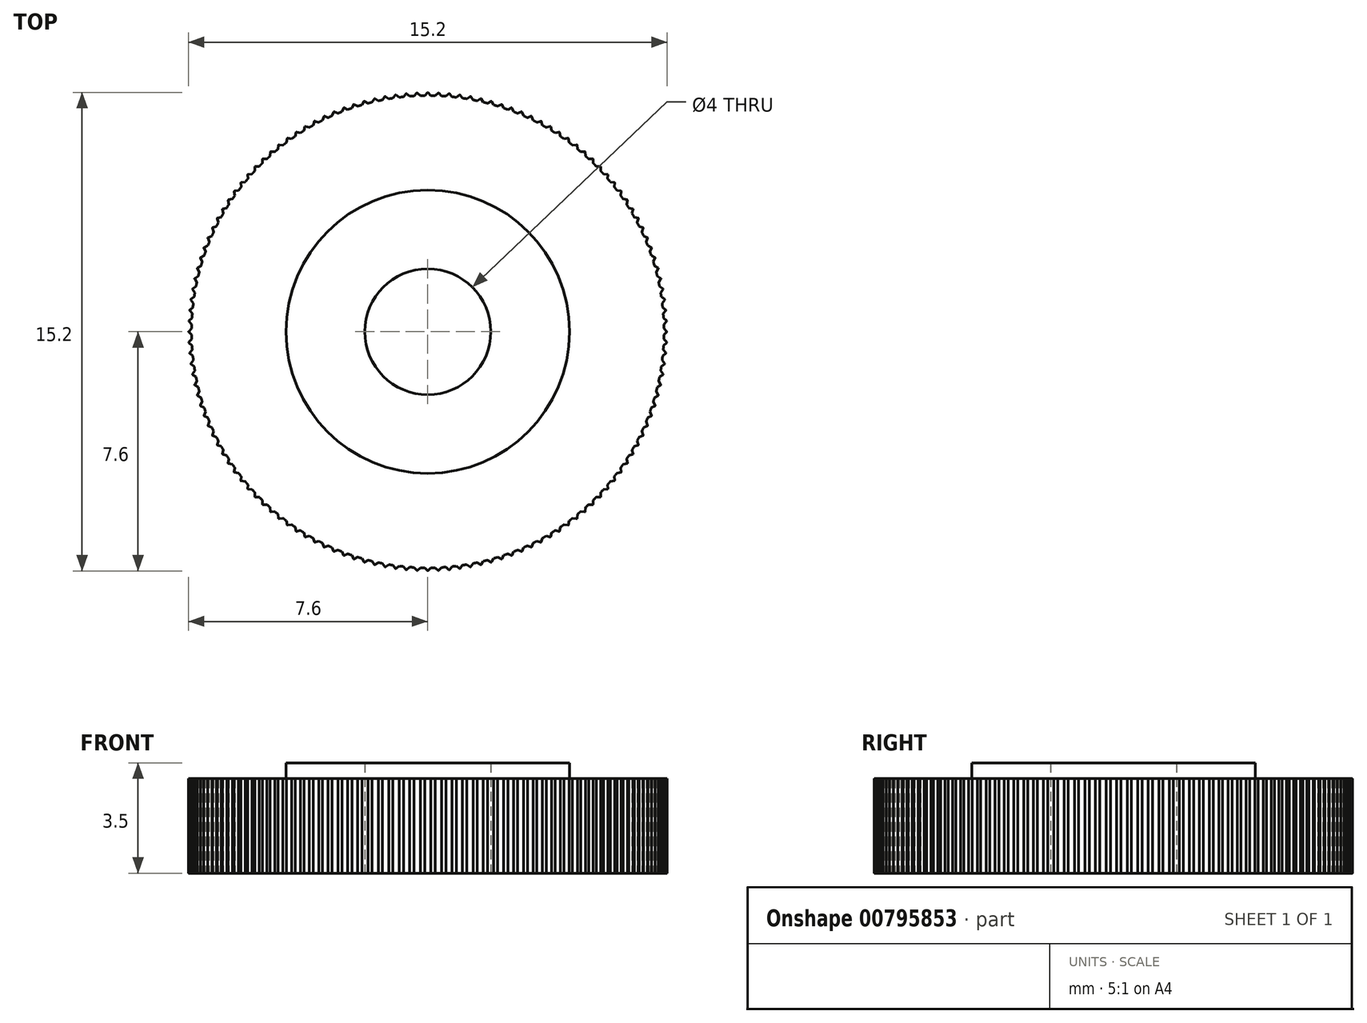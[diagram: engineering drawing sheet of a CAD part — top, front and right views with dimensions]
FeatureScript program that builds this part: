
annotation { "Feature Type Name" : "Feature", "Feature Type Description" : "" }
export const myFeature = defineFeature(function(context is Context, id is Id, definition is map)
    precondition{}
    {
        {
            var Q0;
            Q0=qCreatedBy(makeId("Top.planeOp"),FACE);
            var sketch = newSketch(context, id + "F0", { "sketchPlane" : qUnion([Q0])});
            skCircle(sketch, "E0", {"center": v(0, 0) * mm, "radius": 2 * mm});
            skCircle(sketch, "E1", {"center": v(0, 0) * mm, "radius": 7.5 * mm});
            skArc(sketch, "E2", {"start": v(-0.1, 7.5) * mm, "mid": v(0, 7.5) * mm, "end": v(0.1, 7.5) * mm});
            skLineSegment(sketch, "E3", {"start": v(-0.1, 7.5) * mm, "end": v(0, 7.6) * mm});
            skLineSegment(sketch, "E4", {"start": v(0.1, 7.5) * mm, "end": v(0, 7.6) * mm});
            skPoint(sketch, "E5.visualSharp", {"position": v(0, 7.6) * mm});
            skArc(sketch, "E5.filletArc", {"start": v(0, 7.6) * mm, "mid": v(0, 7.6) * mm, "end": v(0, 7.6) * mm});
            skPoint(sketch, "E6.1.0", {"position": v(-6.58, -3.8) * mm});
            skArc(sketch, "E6.1.1", {"start": v(-6.58, -3.79) * mm, "mid": v(-6.58, -3.8) * mm, "end": v(-6.57, -3.8) * mm});
            skArc(sketch, "E6.2.1", {"start": v(6.57, -3.8) * mm, "mid": v(6.58, -3.8) * mm, "end": v(6.58, -3.79) * mm});
            skLineSegment(sketch, "E7.1.0", {"start": v(-0.44, 7.49) * mm, "end": v(-0.35, 7.58) * mm});
            skArc(sketch, "E7.1.1", {"start": v(-0.44, 7.49) * mm, "mid": v(-0.34, 7.5) * mm, "end": v(-0.24, 7.5) * mm});
            skLineSegment(sketch, "E7.1.2", {"start": v(-0.24, 7.5) * mm, "end": v(-0.33, 7.58) * mm});
            skPoint(sketch, "E7.1.3", {"position": v(-0.34, 7.6) * mm});
            skArc(sketch, "E7.1.4", {"start": v(-0.33, 7.58) * mm, "mid": v(-0.34, 7.59) * mm, "end": v(-0.35, 7.58) * mm});
            skLineSegment(sketch, "E7.2.0", {"start": v(-0.77, 7.46) * mm, "end": v(-0.69, 7.56) * mm});
            skArc(sketch, "E7.2.1", {"start": v(-0.77, 7.46) * mm, "mid": v(-0.67, 7.47) * mm, "end": v(-0.57, 7.48) * mm});
            skLineSegment(sketch, "E7.2.2", {"start": v(-0.57, 7.48) * mm, "end": v(-0.67, 7.56) * mm});
            skPoint(sketch, "E7.2.3", {"position": v(-0.68, 7.57) * mm});
            skArc(sketch, "E7.2.4", {"start": v(-0.67, 7.56) * mm, "mid": v(-0.68, 7.56) * mm, "end": v(-0.69, 7.56) * mm});
            skLineSegment(sketch, "E7.3.0", {"start": v(-1.1, 7.42) * mm, "end": v(-1.03, 7.52) * mm});
            skArc(sketch, "E7.3.1", {"start": v(-1.1, 7.42) * mm, "mid": v(-1, 7.43) * mm, "end": v(-0.9, 7.44) * mm});
            skLineSegment(sketch, "E7.3.2", {"start": v(-0.9, 7.44) * mm, "end": v(-1.01, 7.52) * mm});
            skPoint(sketch, "E7.3.3", {"position": v(-1.02, 7.53) * mm});
            skArc(sketch, "E7.3.4", {"start": v(-1.01, 7.52) * mm, "mid": v(-1.02, 7.53) * mm, "end": v(-1.03, 7.52) * mm});
            skLineSegment(sketch, "E7.4.0", {"start": v(-1.44, 7.36) * mm, "end": v(-1.36, 7.47) * mm});
            skArc(sketch, "E7.4.1", {"start": v(-1.44, 7.36) * mm, "mid": v(-1.34, 7.38) * mm, "end": v(-1.24, 7.4) * mm});
            skLineSegment(sketch, "E7.4.2", {"start": v(-1.24, 7.4) * mm, "end": v(-1.35, 7.47) * mm});
            skPoint(sketch, "E7.4.3", {"position": v(-1.36, 7.48) * mm});
            skArc(sketch, "E7.4.4", {"start": v(-1.35, 7.47) * mm, "mid": v(-1.36, 7.47) * mm, "end": v(-1.36, 7.47) * mm});
            skLineSegment(sketch, "E7.5.0", {"start": v(-1.77, 7.29) * mm, "end": v(-1.7, 7.4) * mm});
            skArc(sketch, "E7.5.1", {"start": v(-1.77, 7.29) * mm, "mid": v(-1.67, 7.31) * mm, "end": v(-1.57, 7.33) * mm});
            skLineSegment(sketch, "E7.5.2", {"start": v(-1.57, 7.33) * mm, "end": v(-1.68, 7.4) * mm});
            skPoint(sketch, "E7.5.3", {"position": v(-1.7, 7.4) * mm});
            skArc(sketch, "E7.5.4", {"start": v(-1.68, 7.4) * mm, "mid": v(-1.7, 7.4) * mm, "end": v(-1.7, 7.4) * mm});
            skLineSegment(sketch, "E7.6.0", {"start": v(-2.1, 7.2) * mm, "end": v(-2.03, 7.32) * mm});
            skArc(sketch, "E7.6.1", {"start": v(-2.1, 7.2) * mm, "mid": v(-2, 7.23) * mm, "end": v(-1.9, 7.26) * mm});
            skLineSegment(sketch, "E7.6.2", {"start": v(-1.9, 7.26) * mm, "end": v(-2.01, 7.32) * mm});
            skPoint(sketch, "E7.6.3", {"position": v(-2.02, 7.33) * mm});
            skArc(sketch, "E7.6.4", {"start": v(-2.01, 7.32) * mm, "mid": v(-2.02, 7.32) * mm, "end": v(-2.03, 7.32) * mm});
            skLineSegment(sketch, "E7.7.0", {"start": v(-2.41, 7.1) * mm, "end": v(-2.35, 7.22) * mm});
            skArc(sketch, "E7.7.1", {"start": v(-2.41, 7.1) * mm, "mid": v(-2.32, 7.13) * mm, "end": v(-2.22, 7.16) * mm});
            skLineSegment(sketch, "E7.7.2", {"start": v(-2.22, 7.16) * mm, "end": v(-2.34, 7.22) * mm});
            skPoint(sketch, "E7.7.3", {"position": v(-2.35, 7.23) * mm});
            skArc(sketch, "E7.7.4", {"start": v(-2.34, 7.22) * mm, "mid": v(-2.35, 7.22) * mm, "end": v(-2.35, 7.22) * mm});
            skLineSegment(sketch, "E7.8.0", {"start": v(-2.73, 6.99) * mm, "end": v(-2.68, 7.1) * mm});
            skArc(sketch, "E7.8.1", {"start": v(-2.73, 6.99) * mm, "mid": v(-2.64, 7.02) * mm, "end": v(-2.54, 7.06) * mm});
            skLineSegment(sketch, "E7.8.2", {"start": v(-2.54, 7.06) * mm, "end": v(-2.66, 7.11) * mm});
            skPoint(sketch, "E7.8.3", {"position": v(-2.67, 7.12) * mm});
            skArc(sketch, "E7.8.4", {"start": v(-2.66, 7.11) * mm, "mid": v(-2.67, 7.11) * mm, "end": v(-2.68, 7.1) * mm});
            skLineSegment(sketch, "E7.9.0", {"start": v(-3.04, 6.86) * mm, "end": v(-3, 6.98) * mm});
            skArc(sketch, "E7.9.1", {"start": v(-3.04, 6.86) * mm, "mid": v(-2.95, 6.9) * mm, "end": v(-2.86, 6.94) * mm});
            skLineSegment(sketch, "E7.9.2", {"start": v(-2.86, 6.94) * mm, "end": v(-2.98, 6.98) * mm});
            skPoint(sketch, "E7.9.3", {"position": v(-2.99, 6.99) * mm});
            skArc(sketch, "E7.9.4", {"start": v(-2.98, 6.98) * mm, "mid": v(-2.99, 6.98) * mm, "end": v(-3, 6.98) * mm});
            skLineSegment(sketch, "E7.10.0", {"start": v(-3.34, 6.71) * mm, "end": v(-3.3, 6.84) * mm});
            skArc(sketch, "E7.10.1", {"start": v(-3.34, 6.71) * mm, "mid": v(-3.25, 6.76) * mm, "end": v(-3.16, 6.8) * mm});
            skLineSegment(sketch, "E7.10.2", {"start": v(-3.16, 6.8) * mm, "end": v(-3.29, 6.84) * mm});
            skPoint(sketch, "E7.10.3", {"position": v(-3.3, 6.85) * mm});
            skArc(sketch, "E7.10.4", {"start": v(-3.29, 6.84) * mm, "mid": v(-3.3, 6.84) * mm, "end": v(-3.3, 6.84) * mm});
            skLineSegment(sketch, "E7.11.0", {"start": v(-3.64, 6.56) * mm, "end": v(-3.6, 6.68) * mm});
            skArc(sketch, "E7.11.1", {"start": v(-3.64, 6.56) * mm, "mid": v(-3.55, 6.6) * mm, "end": v(-3.47, 6.65) * mm});
            skLineSegment(sketch, "E7.11.2", {"start": v(-3.47, 6.65) * mm, "end": v(-3.6, 6.69) * mm});
            skPoint(sketch, "E7.11.3", {"position": v(-3.6, 6.7) * mm});
            skArc(sketch, "E7.11.4", {"start": v(-3.6, 6.69) * mm, "mid": v(-3.6, 6.69) * mm, "end": v(-3.6, 6.68) * mm});
            skLineSegment(sketch, "E7.12.0", {"start": v(-3.93, 6.39) * mm, "end": v(-3.9, 6.51) * mm});
            skArc(sketch, "E7.12.1", {"start": v(-3.93, 6.39) * mm, "mid": v(-3.85, 6.44) * mm, "end": v(-3.76, 6.49) * mm});
            skLineSegment(sketch, "E7.12.2", {"start": v(-3.76, 6.49) * mm, "end": v(-3.89, 6.52) * mm});
            skPoint(sketch, "E7.12.3", {"position": v(-3.9, 6.52) * mm});
            skArc(sketch, "E7.12.4", {"start": v(-3.89, 6.52) * mm, "mid": v(-3.9, 6.52) * mm, "end": v(-3.9, 6.51) * mm});
            skLineSegment(sketch, "E7.13.0", {"start": v(-4.21, 6.2) * mm, "end": v(-4.19, 6.33) * mm});
            skArc(sketch, "E7.13.1", {"start": v(-4.21, 6.2) * mm, "mid": v(-4.13, 6.26) * mm, "end": v(-4.05, 6.31) * mm});
            skLineSegment(sketch, "E7.13.2", {"start": v(-4.05, 6.31) * mm, "end": v(-4.18, 6.34) * mm});
            skPoint(sketch, "E7.13.3", {"position": v(-4.19, 6.34) * mm});
            skArc(sketch, "E7.13.4", {"start": v(-4.18, 6.34) * mm, "mid": v(-4.18, 6.34) * mm, "end": v(-4.19, 6.33) * mm});
            skLineSegment(sketch, "E7.14.0", {"start": v(-4.49, 6) * mm, "end": v(-4.47, 6.14) * mm});
            skArc(sketch, "E7.14.1", {"start": v(-4.49, 6) * mm, "mid": v(-4.4, 6.07) * mm, "end": v(-4.33, 6.13) * mm});
            skLineSegment(sketch, "E7.14.2", {"start": v(-4.33, 6.13) * mm, "end": v(-4.46, 6.15) * mm});
            skPoint(sketch, "E7.14.3", {"position": v(-4.47, 6.15) * mm});
            skArc(sketch, "E7.14.4", {"start": v(-4.46, 6.15) * mm, "mid": v(-4.46, 6.14) * mm, "end": v(-4.47, 6.14) * mm});
            skLineSegment(sketch, "E7.15.0", {"start": v(-4.75, 5.8) * mm, "end": v(-4.74, 5.93) * mm});
            skArc(sketch, "E7.15.1", {"start": v(-4.75, 5.8) * mm, "mid": v(-4.68, 5.86) * mm, "end": v(-4.6, 5.93) * mm});
            skLineSegment(sketch, "E7.15.2", {"start": v(-4.6, 5.93) * mm, "end": v(-4.73, 5.94) * mm});
            skPoint(sketch, "E7.15.3", {"position": v(-4.74, 5.94) * mm});
            skArc(sketch, "E7.15.4", {"start": v(-4.73, 5.94) * mm, "mid": v(-4.74, 5.94) * mm, "end": v(-4.74, 5.93) * mm});
            skLineSegment(sketch, "E7.16.0", {"start": v(-5, 5.58) * mm, "end": v(-5, 5.71) * mm});
            skArc(sketch, "E7.16.1", {"start": v(-5, 5.58) * mm, "mid": v(-4.93, 5.65) * mm, "end": v(-4.86, 5.71) * mm});
            skLineSegment(sketch, "E7.16.2", {"start": v(-4.86, 5.71) * mm, "end": v(-4.99, 5.72) * mm});
            skPoint(sketch, "E7.16.3", {"position": v(-5, 5.72) * mm});
            skArc(sketch, "E7.16.4", {"start": v(-4.99, 5.72) * mm, "mid": v(-5, 5.72) * mm, "end": v(-5, 5.71) * mm});
            skLineSegment(sketch, "E7.17.0", {"start": v(-5.25, 5.35) * mm, "end": v(-5.25, 5.48) * mm});
            skArc(sketch, "E7.17.1", {"start": v(-5.25, 5.35) * mm, "mid": v(-5.18, 5.42) * mm, "end": v(-5.11, 5.49) * mm});
            skLineSegment(sketch, "E7.17.2", {"start": v(-5.11, 5.49) * mm, "end": v(-5.24, 5.5) * mm});
            skPoint(sketch, "E7.17.3", {"position": v(-5.25, 5.5) * mm});
            skArc(sketch, "E7.17.4", {"start": v(-5.24, 5.5) * mm, "mid": v(-5.25, 5.49) * mm, "end": v(-5.25, 5.48) * mm});
            skLineSegment(sketch, "E7.18.0", {"start": v(-5.49, 5.11) * mm, "end": v(-5.5, 5.24) * mm});
            skArc(sketch, "E7.18.1", {"start": v(-5.49, 5.11) * mm, "mid": v(-5.42, 5.18) * mm, "end": v(-5.35, 5.25) * mm});
            skLineSegment(sketch, "E7.18.2", {"start": v(-5.35, 5.25) * mm, "end": v(-5.48, 5.25) * mm});
            skPoint(sketch, "E7.18.3", {"position": v(-5.5, 5.25) * mm});
            skArc(sketch, "E7.18.4", {"start": v(-5.48, 5.25) * mm, "mid": v(-5.49, 5.25) * mm, "end": v(-5.5, 5.24) * mm});
            skLineSegment(sketch, "E7.19.0", {"start": v(-5.71, 4.86) * mm, "end": v(-5.72, 4.99) * mm});
            skArc(sketch, "E7.19.1", {"start": v(-5.71, 4.86) * mm, "mid": v(-5.65, 4.93) * mm, "end": v(-5.58, 5) * mm});
            skLineSegment(sketch, "E7.19.2", {"start": v(-5.58, 5) * mm, "end": v(-5.71, 5) * mm});
            skPoint(sketch, "E7.19.3", {"position": v(-5.72, 5) * mm});
            skArc(sketch, "E7.19.4", {"start": v(-5.71, 5) * mm, "mid": v(-5.72, 5) * mm, "end": v(-5.72, 4.99) * mm});
            skLineSegment(sketch, "E7.20.0", {"start": v(-5.93, 4.6) * mm, "end": v(-5.94, 4.73) * mm});
            skArc(sketch, "E7.20.1", {"start": v(-5.93, 4.6) * mm, "mid": v(-5.86, 4.68) * mm, "end": v(-5.8, 4.75) * mm});
            skLineSegment(sketch, "E7.20.2", {"start": v(-5.8, 4.75) * mm, "end": v(-5.93, 4.74) * mm});
            skPoint(sketch, "E7.20.3", {"position": v(-5.94, 4.74) * mm});
            skArc(sketch, "E7.20.4", {"start": v(-5.93, 4.74) * mm, "mid": v(-5.94, 4.74) * mm, "end": v(-5.94, 4.73) * mm});
            skLineSegment(sketch, "E7.21.0", {"start": v(-6.13, 4.33) * mm, "end": v(-6.15, 4.46) * mm});
            skArc(sketch, "E7.21.1", {"start": v(-6.13, 4.33) * mm, "mid": v(-6.07, 4.4) * mm, "end": v(-6, 4.49) * mm});
            skLineSegment(sketch, "E7.21.2", {"start": v(-6, 4.49) * mm, "end": v(-6.14, 4.47) * mm});
            skPoint(sketch, "E7.21.3", {"position": v(-6.15, 4.47) * mm});
            skArc(sketch, "E7.21.4", {"start": v(-6.14, 4.47) * mm, "mid": v(-6.14, 4.46) * mm, "end": v(-6.15, 4.46) * mm});
            skLineSegment(sketch, "E7.22.0", {"start": v(-6.31, 4.05) * mm, "end": v(-6.34, 4.18) * mm});
            skArc(sketch, "E7.22.1", {"start": v(-6.31, 4.05) * mm, "mid": v(-6.26, 4.13) * mm, "end": v(-6.2, 4.21) * mm});
            skLineSegment(sketch, "E7.22.2", {"start": v(-6.2, 4.21) * mm, "end": v(-6.33, 4.19) * mm});
            skPoint(sketch, "E7.22.3", {"position": v(-6.34, 4.19) * mm});
            skArc(sketch, "E7.22.4", {"start": v(-6.33, 4.19) * mm, "mid": v(-6.34, 4.18) * mm, "end": v(-6.34, 4.18) * mm});
            skLineSegment(sketch, "E7.23.0", {"start": v(-6.49, 3.76) * mm, "end": v(-6.52, 3.89) * mm});
            skArc(sketch, "E7.23.1", {"start": v(-6.49, 3.76) * mm, "mid": v(-6.44, 3.85) * mm, "end": v(-6.39, 3.93) * mm});
            skLineSegment(sketch, "E7.23.2", {"start": v(-6.39, 3.93) * mm, "end": v(-6.51, 3.9) * mm});
            skPoint(sketch, "E7.23.3", {"position": v(-6.52, 3.9) * mm});
            skArc(sketch, "E7.23.4", {"start": v(-6.51, 3.9) * mm, "mid": v(-6.52, 3.9) * mm, "end": v(-6.52, 3.89) * mm});
            skLineSegment(sketch, "E7.24.0", {"start": v(-6.65, 3.47) * mm, "end": v(-6.69, 3.6) * mm});
            skArc(sketch, "E7.24.1", {"start": v(-6.65, 3.47) * mm, "mid": v(-6.6, 3.55) * mm, "end": v(-6.56, 3.64) * mm});
            skLineSegment(sketch, "E7.24.2", {"start": v(-6.56, 3.64) * mm, "end": v(-6.68, 3.6) * mm});
            skPoint(sketch, "E7.24.3", {"position": v(-6.7, 3.6) * mm});
            skArc(sketch, "E7.24.4", {"start": v(-6.68, 3.6) * mm, "mid": v(-6.69, 3.6) * mm, "end": v(-6.69, 3.6) * mm});
            skLineSegment(sketch, "E7.25.0", {"start": v(-6.8, 3.16) * mm, "end": v(-6.84, 3.29) * mm});
            skArc(sketch, "E7.25.1", {"start": v(-6.8, 3.16) * mm, "mid": v(-6.76, 3.25) * mm, "end": v(-6.71, 3.34) * mm});
            skLineSegment(sketch, "E7.25.2", {"start": v(-6.71, 3.34) * mm, "end": v(-6.84, 3.3) * mm});
            skPoint(sketch, "E7.25.3", {"position": v(-6.85, 3.3) * mm});
            skArc(sketch, "E7.25.4", {"start": v(-6.84, 3.3) * mm, "mid": v(-6.84, 3.3) * mm, "end": v(-6.84, 3.29) * mm});
            skLineSegment(sketch, "E7.26.0", {"start": v(-6.94, 2.86) * mm, "end": v(-6.98, 2.98) * mm});
            skArc(sketch, "E7.26.1", {"start": v(-6.94, 2.86) * mm, "mid": v(-6.9, 2.95) * mm, "end": v(-6.86, 3.04) * mm});
            skLineSegment(sketch, "E7.26.2", {"start": v(-6.86, 3.04) * mm, "end": v(-6.98, 3) * mm});
            skPoint(sketch, "E7.26.3", {"position": v(-6.99, 2.99) * mm});
            skArc(sketch, "E7.26.4", {"start": v(-6.98, 3) * mm, "mid": v(-6.98, 2.99) * mm, "end": v(-6.98, 2.98) * mm});
            skLineSegment(sketch, "E7.27.0", {"start": v(-7.06, 2.54) * mm, "end": v(-7.11, 2.66) * mm});
            skArc(sketch, "E7.27.1", {"start": v(-7.06, 2.54) * mm, "mid": v(-7.02, 2.64) * mm, "end": v(-6.99, 2.73) * mm});
            skLineSegment(sketch, "E7.27.2", {"start": v(-6.99, 2.73) * mm, "end": v(-7.1, 2.68) * mm});
            skPoint(sketch, "E7.27.3", {"position": v(-7.12, 2.67) * mm});
            skArc(sketch, "E7.27.4", {"start": v(-7.1, 2.68) * mm, "mid": v(-7.11, 2.67) * mm, "end": v(-7.11, 2.66) * mm});
            skLineSegment(sketch, "E7.28.0", {"start": v(-7.16, 2.22) * mm, "end": v(-7.22, 2.34) * mm});
            skArc(sketch, "E7.28.1", {"start": v(-7.16, 2.22) * mm, "mid": v(-7.13, 2.32) * mm, "end": v(-7.1, 2.41) * mm});
            skLineSegment(sketch, "E7.28.2", {"start": v(-7.1, 2.41) * mm, "end": v(-7.22, 2.35) * mm});
            skPoint(sketch, "E7.28.3", {"position": v(-7.23, 2.35) * mm});
            skArc(sketch, "E7.28.4", {"start": v(-7.22, 2.35) * mm, "mid": v(-7.22, 2.35) * mm, "end": v(-7.22, 2.34) * mm});
            skLineSegment(sketch, "E7.29.0", {"start": v(-7.26, 1.9) * mm, "end": v(-7.32, 2.01) * mm});
            skArc(sketch, "E7.29.1", {"start": v(-7.26, 1.9) * mm, "mid": v(-7.23, 2) * mm, "end": v(-7.2, 2.1) * mm});
            skLineSegment(sketch, "E7.29.2", {"start": v(-7.2, 2.1) * mm, "end": v(-7.32, 2.03) * mm});
            skPoint(sketch, "E7.29.3", {"position": v(-7.33, 2.02) * mm});
            skArc(sketch, "E7.29.4", {"start": v(-7.32, 2.03) * mm, "mid": v(-7.32, 2.02) * mm, "end": v(-7.32, 2.01) * mm});
            skLineSegment(sketch, "E7.30.0", {"start": v(-7.33, 1.57) * mm, "end": v(-7.4, 1.68) * mm});
            skArc(sketch, "E7.30.1", {"start": v(-7.33, 1.57) * mm, "mid": v(-7.31, 1.67) * mm, "end": v(-7.29, 1.77) * mm});
            skLineSegment(sketch, "E7.30.2", {"start": v(-7.29, 1.77) * mm, "end": v(-7.4, 1.7) * mm});
            skPoint(sketch, "E7.30.3", {"position": v(-7.4, 1.7) * mm});
            skArc(sketch, "E7.30.4", {"start": v(-7.4, 1.7) * mm, "mid": v(-7.4, 1.7) * mm, "end": v(-7.4, 1.68) * mm});
            skLineSegment(sketch, "E7.31.0", {"start": v(-7.4, 1.24) * mm, "end": v(-7.47, 1.35) * mm});
            skArc(sketch, "E7.31.1", {"start": v(-7.4, 1.24) * mm, "mid": v(-7.38, 1.34) * mm, "end": v(-7.36, 1.44) * mm});
            skLineSegment(sketch, "E7.31.2", {"start": v(-7.36, 1.44) * mm, "end": v(-7.47, 1.36) * mm});
            skPoint(sketch, "E7.31.3", {"position": v(-7.48, 1.36) * mm});
            skArc(sketch, "E7.31.4", {"start": v(-7.47, 1.36) * mm, "mid": v(-7.47, 1.36) * mm, "end": v(-7.47, 1.35) * mm});
            skLineSegment(sketch, "E7.32.0", {"start": v(-7.44, 0.9) * mm, "end": v(-7.52, 1.01) * mm});
            skArc(sketch, "E7.32.1", {"start": v(-7.44, 0.9) * mm, "mid": v(-7.43, 1) * mm, "end": v(-7.42, 1.1) * mm});
            skLineSegment(sketch, "E7.32.2", {"start": v(-7.42, 1.1) * mm, "end": v(-7.52, 1.03) * mm});
            skPoint(sketch, "E7.32.3", {"position": v(-7.53, 1.02) * mm});
            skArc(sketch, "E7.32.4", {"start": v(-7.52, 1.03) * mm, "mid": v(-7.53, 1.02) * mm, "end": v(-7.52, 1.01) * mm});
            skLineSegment(sketch, "E7.33.0", {"start": v(-7.48, 0.57) * mm, "end": v(-7.56, 0.67) * mm});
            skArc(sketch, "E7.33.1", {"start": v(-7.48, 0.57) * mm, "mid": v(-7.47, 0.67) * mm, "end": v(-7.46, 0.77) * mm});
            skLineSegment(sketch, "E7.33.2", {"start": v(-7.46, 0.77) * mm, "end": v(-7.56, 0.69) * mm});
            skPoint(sketch, "E7.33.3", {"position": v(-7.57, 0.68) * mm});
            skArc(sketch, "E7.33.4", {"start": v(-7.56, 0.69) * mm, "mid": v(-7.56, 0.68) * mm, "end": v(-7.56, 0.67) * mm});
            skLineSegment(sketch, "E7.34.0", {"start": v(-7.5, 0.24) * mm, "end": v(-7.58, 0.33) * mm});
            skArc(sketch, "E7.34.1", {"start": v(-7.5, 0.24) * mm, "mid": v(-7.5, 0.34) * mm, "end": v(-7.49, 0.44) * mm});
            skLineSegment(sketch, "E7.34.2", {"start": v(-7.49, 0.44) * mm, "end": v(-7.58, 0.35) * mm});
            skPoint(sketch, "E7.34.3", {"position": v(-7.6, 0.34) * mm});
            skArc(sketch, "E7.34.4", {"start": v(-7.58, 0.35) * mm, "mid": v(-7.59, 0.34) * mm, "end": v(-7.58, 0.33) * mm});
            skLineSegment(sketch, "E7.35.0", {"start": v(-7.5, -0.1) * mm, "end": v(-7.6, 0) * mm});
            skArc(sketch, "E7.35.1", {"start": v(-7.5, -0.1) * mm, "mid": v(-7.5, 0) * mm, "end": v(-7.5, 0.1) * mm});
            skLineSegment(sketch, "E7.35.2", {"start": v(-7.5, 0.1) * mm, "end": v(-7.6, 0) * mm});
            skPoint(sketch, "E7.35.3", {"position": v(-7.6, 0) * mm});
            skArc(sketch, "E7.35.4", {"start": v(-7.6, 0) * mm, "mid": v(-7.6, 0) * mm, "end": v(-7.6, 0) * mm});
            skLineSegment(sketch, "E7.36.0", {"start": v(-7.49, -0.44) * mm, "end": v(-7.58, -0.35) * mm});
            skArc(sketch, "E7.36.1", {"start": v(-7.49, -0.44) * mm, "mid": v(-7.5, -0.34) * mm, "end": v(-7.5, -0.24) * mm});
            skLineSegment(sketch, "E7.36.2", {"start": v(-7.5, -0.24) * mm, "end": v(-7.58, -0.33) * mm});
            skPoint(sketch, "E7.36.3", {"position": v(-7.6, -0.34) * mm});
            skArc(sketch, "E7.36.4", {"start": v(-7.58, -0.33) * mm, "mid": v(-7.59, -0.34) * mm, "end": v(-7.58, -0.35) * mm});
            skLineSegment(sketch, "E7.37.0", {"start": v(-7.46, -0.77) * mm, "end": v(-7.56, -0.69) * mm});
            skArc(sketch, "E7.37.1", {"start": v(-7.46, -0.77) * mm, "mid": v(-7.47, -0.67) * mm, "end": v(-7.48, -0.57) * mm});
            skLineSegment(sketch, "E7.37.2", {"start": v(-7.48, -0.57) * mm, "end": v(-7.56, -0.67) * mm});
            skPoint(sketch, "E7.37.3", {"position": v(-7.57, -0.68) * mm});
            skArc(sketch, "E7.37.4", {"start": v(-7.56, -0.67) * mm, "mid": v(-7.56, -0.68) * mm, "end": v(-7.56, -0.69) * mm});
            skLineSegment(sketch, "E7.38.0", {"start": v(-7.42, -1.1) * mm, "end": v(-7.52, -1.03) * mm});
            skArc(sketch, "E7.38.1", {"start": v(-7.42, -1.1) * mm, "mid": v(-7.43, -1) * mm, "end": v(-7.44, -0.9) * mm});
            skLineSegment(sketch, "E7.38.2", {"start": v(-7.44, -0.9) * mm, "end": v(-7.52, -1.01) * mm});
            skPoint(sketch, "E7.38.3", {"position": v(-7.53, -1.02) * mm});
            skArc(sketch, "E7.38.4", {"start": v(-7.52, -1.01) * mm, "mid": v(-7.53, -1.02) * mm, "end": v(-7.52, -1.03) * mm});
            skLineSegment(sketch, "E7.39.0", {"start": v(-7.36, -1.44) * mm, "end": v(-7.47, -1.36) * mm});
            skArc(sketch, "E7.39.1", {"start": v(-7.36, -1.44) * mm, "mid": v(-7.38, -1.34) * mm, "end": v(-7.4, -1.24) * mm});
            skLineSegment(sketch, "E7.39.2", {"start": v(-7.4, -1.24) * mm, "end": v(-7.47, -1.35) * mm});
            skPoint(sketch, "E7.39.3", {"position": v(-7.48, -1.36) * mm});
            skArc(sketch, "E7.39.4", {"start": v(-7.47, -1.35) * mm, "mid": v(-7.47, -1.36) * mm, "end": v(-7.47, -1.36) * mm});
            skLineSegment(sketch, "E7.40.0", {"start": v(-7.29, -1.77) * mm, "end": v(-7.4, -1.7) * mm});
            skArc(sketch, "E7.40.1", {"start": v(-7.29, -1.77) * mm, "mid": v(-7.31, -1.67) * mm, "end": v(-7.33, -1.57) * mm});
            skLineSegment(sketch, "E7.40.2", {"start": v(-7.33, -1.57) * mm, "end": v(-7.4, -1.68) * mm});
            skPoint(sketch, "E7.40.3", {"position": v(-7.4, -1.7) * mm});
            skArc(sketch, "E7.40.4", {"start": v(-7.4, -1.68) * mm, "mid": v(-7.4, -1.7) * mm, "end": v(-7.4, -1.7) * mm});
            skLineSegment(sketch, "E7.41.0", {"start": v(-7.2, -2.1) * mm, "end": v(-7.32, -2.03) * mm});
            skArc(sketch, "E7.41.1", {"start": v(-7.2, -2.1) * mm, "mid": v(-7.23, -2) * mm, "end": v(-7.26, -1.9) * mm});
            skLineSegment(sketch, "E7.41.2", {"start": v(-7.26, -1.9) * mm, "end": v(-7.32, -2.01) * mm});
            skPoint(sketch, "E7.41.3", {"position": v(-7.33, -2.02) * mm});
            skArc(sketch, "E7.41.4", {"start": v(-7.32, -2.01) * mm, "mid": v(-7.32, -2.02) * mm, "end": v(-7.32, -2.03) * mm});
            skLineSegment(sketch, "E7.42.0", {"start": v(-7.1, -2.41) * mm, "end": v(-7.22, -2.35) * mm});
            skArc(sketch, "E7.42.1", {"start": v(-7.1, -2.41) * mm, "mid": v(-7.13, -2.32) * mm, "end": v(-7.16, -2.22) * mm});
            skLineSegment(sketch, "E7.42.2", {"start": v(-7.16, -2.22) * mm, "end": v(-7.22, -2.34) * mm});
            skPoint(sketch, "E7.42.3", {"position": v(-7.23, -2.35) * mm});
            skArc(sketch, "E7.42.4", {"start": v(-7.22, -2.34) * mm, "mid": v(-7.22, -2.35) * mm, "end": v(-7.22, -2.35) * mm});
            skLineSegment(sketch, "E7.43.0", {"start": v(-6.99, -2.73) * mm, "end": v(-7.1, -2.68) * mm});
            skArc(sketch, "E7.43.1", {"start": v(-6.99, -2.73) * mm, "mid": v(-7.02, -2.64) * mm, "end": v(-7.06, -2.54) * mm});
            skLineSegment(sketch, "E7.43.2", {"start": v(-7.06, -2.54) * mm, "end": v(-7.11, -2.66) * mm});
            skPoint(sketch, "E7.43.3", {"position": v(-7.12, -2.67) * mm});
            skArc(sketch, "E7.43.4", {"start": v(-7.11, -2.66) * mm, "mid": v(-7.11, -2.67) * mm, "end": v(-7.1, -2.68) * mm});
            skLineSegment(sketch, "E7.44.0", {"start": v(-6.86, -3.04) * mm, "end": v(-6.98, -3) * mm});
            skArc(sketch, "E7.44.1", {"start": v(-6.86, -3.04) * mm, "mid": v(-6.9, -2.95) * mm, "end": v(-6.94, -2.86) * mm});
            skLineSegment(sketch, "E7.44.2", {"start": v(-6.94, -2.86) * mm, "end": v(-6.98, -2.98) * mm});
            skPoint(sketch, "E7.44.3", {"position": v(-6.99, -2.99) * mm});
            skArc(sketch, "E7.44.4", {"start": v(-6.98, -2.98) * mm, "mid": v(-6.98, -2.99) * mm, "end": v(-6.98, -3) * mm});
            skLineSegment(sketch, "E7.45.0", {"start": v(-6.71, -3.34) * mm, "end": v(-6.84, -3.3) * mm});
            skArc(sketch, "E7.45.1", {"start": v(-6.71, -3.34) * mm, "mid": v(-6.76, -3.25) * mm, "end": v(-6.8, -3.16) * mm});
            skLineSegment(sketch, "E7.45.2", {"start": v(-6.8, -3.16) * mm, "end": v(-6.84, -3.29) * mm});
            skPoint(sketch, "E7.45.3", {"position": v(-6.85, -3.3) * mm});
            skArc(sketch, "E7.45.4", {"start": v(-6.84, -3.29) * mm, "mid": v(-6.84, -3.3) * mm, "end": v(-6.84, -3.3) * mm});
            skLineSegment(sketch, "E7.46.0", {"start": v(-6.56, -3.64) * mm, "end": v(-6.68, -3.6) * mm});
            skArc(sketch, "E7.46.1", {"start": v(-6.56, -3.64) * mm, "mid": v(-6.6, -3.55) * mm, "end": v(-6.65, -3.47) * mm});
            skLineSegment(sketch, "E7.46.2", {"start": v(-6.65, -3.47) * mm, "end": v(-6.69, -3.6) * mm});
            skPoint(sketch, "E7.46.3", {"position": v(-6.7, -3.6) * mm});
            skArc(sketch, "E7.46.4", {"start": v(-6.69, -3.6) * mm, "mid": v(-6.69, -3.6) * mm, "end": v(-6.68, -3.6) * mm});
            skLineSegment(sketch, "E7.47.0", {"start": v(-6.39, -3.93) * mm, "end": v(-6.51, -3.9) * mm});
            skArc(sketch, "E7.47.1", {"start": v(-6.39, -3.93) * mm, "mid": v(-6.44, -3.85) * mm, "end": v(-6.49, -3.76) * mm});
            skLineSegment(sketch, "E7.47.2", {"start": v(-6.49, -3.76) * mm, "end": v(-6.52, -3.89) * mm});
            skPoint(sketch, "E7.47.3", {"position": v(-6.52, -3.9) * mm});
            skArc(sketch, "E7.47.4", {"start": v(-6.52, -3.89) * mm, "mid": v(-6.52, -3.9) * mm, "end": v(-6.51, -3.9) * mm});
            skLineSegment(sketch, "E7.48.0", {"start": v(-6.2, -4.21) * mm, "end": v(-6.33, -4.19) * mm});
            skArc(sketch, "E7.48.1", {"start": v(-6.2, -4.21) * mm, "mid": v(-6.26, -4.13) * mm, "end": v(-6.31, -4.05) * mm});
            skLineSegment(sketch, "E7.48.2", {"start": v(-6.31, -4.05) * mm, "end": v(-6.34, -4.18) * mm});
            skPoint(sketch, "E7.48.3", {"position": v(-6.34, -4.19) * mm});
            skArc(sketch, "E7.48.4", {"start": v(-6.34, -4.18) * mm, "mid": v(-6.34, -4.18) * mm, "end": v(-6.33, -4.19) * mm});
            skLineSegment(sketch, "E7.49.0", {"start": v(-6, -4.49) * mm, "end": v(-6.14, -4.47) * mm});
            skArc(sketch, "E7.49.1", {"start": v(-6, -4.49) * mm, "mid": v(-6.07, -4.4) * mm, "end": v(-6.13, -4.33) * mm});
            skLineSegment(sketch, "E7.49.2", {"start": v(-6.13, -4.33) * mm, "end": v(-6.15, -4.46) * mm});
            skPoint(sketch, "E7.49.3", {"position": v(-6.15, -4.47) * mm});
            skArc(sketch, "E7.49.4", {"start": v(-6.15, -4.46) * mm, "mid": v(-6.14, -4.46) * mm, "end": v(-6.14, -4.47) * mm});
            skLineSegment(sketch, "E7.50.0", {"start": v(-5.8, -4.75) * mm, "end": v(-5.93, -4.74) * mm});
            skArc(sketch, "E7.50.1", {"start": v(-5.8, -4.75) * mm, "mid": v(-5.86, -4.68) * mm, "end": v(-5.93, -4.6) * mm});
            skLineSegment(sketch, "E7.50.2", {"start": v(-5.93, -4.6) * mm, "end": v(-5.94, -4.73) * mm});
            skPoint(sketch, "E7.50.3", {"position": v(-5.94, -4.74) * mm});
            skArc(sketch, "E7.50.4", {"start": v(-5.94, -4.73) * mm, "mid": v(-5.94, -4.74) * mm, "end": v(-5.93, -4.74) * mm});
            skLineSegment(sketch, "E7.51.0", {"start": v(-5.58, -5) * mm, "end": v(-5.71, -5) * mm});
            skArc(sketch, "E7.51.1", {"start": v(-5.58, -5) * mm, "mid": v(-5.65, -4.93) * mm, "end": v(-5.71, -4.86) * mm});
            skLineSegment(sketch, "E7.51.2", {"start": v(-5.71, -4.86) * mm, "end": v(-5.72, -4.99) * mm});
            skPoint(sketch, "E7.51.3", {"position": v(-5.72, -5) * mm});
            skArc(sketch, "E7.51.4", {"start": v(-5.72, -4.99) * mm, "mid": v(-5.72, -5) * mm, "end": v(-5.71, -5) * mm});
            skLineSegment(sketch, "E7.52.0", {"start": v(-5.35, -5.25) * mm, "end": v(-5.48, -5.25) * mm});
            skArc(sketch, "E7.52.1", {"start": v(-5.35, -5.25) * mm, "mid": v(-5.42, -5.18) * mm, "end": v(-5.49, -5.11) * mm});
            skLineSegment(sketch, "E7.52.2", {"start": v(-5.49, -5.11) * mm, "end": v(-5.5, -5.24) * mm});
            skPoint(sketch, "E7.52.3", {"position": v(-5.5, -5.25) * mm});
            skArc(sketch, "E7.52.4", {"start": v(-5.5, -5.24) * mm, "mid": v(-5.49, -5.25) * mm, "end": v(-5.48, -5.25) * mm});
            skLineSegment(sketch, "E7.53.0", {"start": v(-5.11, -5.49) * mm, "end": v(-5.24, -5.5) * mm});
            skArc(sketch, "E7.53.1", {"start": v(-5.11, -5.49) * mm, "mid": v(-5.18, -5.42) * mm, "end": v(-5.25, -5.35) * mm});
            skLineSegment(sketch, "E7.53.2", {"start": v(-5.25, -5.35) * mm, "end": v(-5.25, -5.48) * mm});
            skPoint(sketch, "E7.53.3", {"position": v(-5.25, -5.5) * mm});
            skArc(sketch, "E7.53.4", {"start": v(-5.25, -5.48) * mm, "mid": v(-5.25, -5.49) * mm, "end": v(-5.24, -5.5) * mm});
            skLineSegment(sketch, "E7.54.0", {"start": v(-4.86, -5.71) * mm, "end": v(-4.99, -5.72) * mm});
            skArc(sketch, "E7.54.1", {"start": v(-4.86, -5.71) * mm, "mid": v(-4.93, -5.65) * mm, "end": v(-5, -5.58) * mm});
            skLineSegment(sketch, "E7.54.2", {"start": v(-5, -5.58) * mm, "end": v(-5, -5.71) * mm});
            skPoint(sketch, "E7.54.3", {"position": v(-5, -5.72) * mm});
            skArc(sketch, "E7.54.4", {"start": v(-5, -5.71) * mm, "mid": v(-5, -5.72) * mm, "end": v(-4.99, -5.72) * mm});
            skLineSegment(sketch, "E7.55.0", {"start": v(-4.6, -5.93) * mm, "end": v(-4.73, -5.94) * mm});
            skArc(sketch, "E7.55.1", {"start": v(-4.6, -5.93) * mm, "mid": v(-4.68, -5.86) * mm, "end": v(-4.75, -5.8) * mm});
            skLineSegment(sketch, "E7.55.2", {"start": v(-4.75, -5.8) * mm, "end": v(-4.74, -5.93) * mm});
            skPoint(sketch, "E7.55.3", {"position": v(-4.74, -5.94) * mm});
            skArc(sketch, "E7.55.4", {"start": v(-4.74, -5.93) * mm, "mid": v(-4.74, -5.94) * mm, "end": v(-4.73, -5.94) * mm});
            skLineSegment(sketch, "E7.56.0", {"start": v(-4.33, -6.13) * mm, "end": v(-4.46, -6.15) * mm});
            skArc(sketch, "E7.56.1", {"start": v(-4.33, -6.13) * mm, "mid": v(-4.4, -6.07) * mm, "end": v(-4.49, -6) * mm});
            skLineSegment(sketch, "E7.56.2", {"start": v(-4.49, -6) * mm, "end": v(-4.47, -6.14) * mm});
            skPoint(sketch, "E7.56.3", {"position": v(-4.47, -6.15) * mm});
            skArc(sketch, "E7.56.4", {"start": v(-4.47, -6.14) * mm, "mid": v(-4.46, -6.14) * mm, "end": v(-4.46, -6.15) * mm});
            skLineSegment(sketch, "E7.57.0", {"start": v(-4.05, -6.31) * mm, "end": v(-4.18, -6.34) * mm});
            skArc(sketch, "E7.57.1", {"start": v(-4.05, -6.31) * mm, "mid": v(-4.13, -6.26) * mm, "end": v(-4.21, -6.2) * mm});
            skLineSegment(sketch, "E7.57.2", {"start": v(-4.21, -6.2) * mm, "end": v(-4.19, -6.33) * mm});
            skPoint(sketch, "E7.57.3", {"position": v(-4.19, -6.34) * mm});
            skArc(sketch, "E7.57.4", {"start": v(-4.19, -6.33) * mm, "mid": v(-4.18, -6.34) * mm, "end": v(-4.18, -6.34) * mm});
            skLineSegment(sketch, "E7.58.0", {"start": v(-3.76, -6.49) * mm, "end": v(-3.89, -6.52) * mm});
            skArc(sketch, "E7.58.1", {"start": v(-3.76, -6.49) * mm, "mid": v(-3.85, -6.44) * mm, "end": v(-3.93, -6.39) * mm});
            skLineSegment(sketch, "E7.58.2", {"start": v(-3.93, -6.39) * mm, "end": v(-3.9, -6.51) * mm});
            skPoint(sketch, "E7.58.3", {"position": v(-3.9, -6.52) * mm});
            skArc(sketch, "E7.58.4", {"start": v(-3.9, -6.51) * mm, "mid": v(-3.9, -6.52) * mm, "end": v(-3.89, -6.52) * mm});
            skLineSegment(sketch, "E7.59.0", {"start": v(-3.47, -6.65) * mm, "end": v(-3.6, -6.69) * mm});
            skArc(sketch, "E7.59.1", {"start": v(-3.47, -6.65) * mm, "mid": v(-3.55, -6.6) * mm, "end": v(-3.64, -6.56) * mm});
            skLineSegment(sketch, "E7.59.2", {"start": v(-3.64, -6.56) * mm, "end": v(-3.6, -6.68) * mm});
            skPoint(sketch, "E7.59.3", {"position": v(-3.6, -6.7) * mm});
            skArc(sketch, "E7.59.4", {"start": v(-3.6, -6.68) * mm, "mid": v(-3.6, -6.69) * mm, "end": v(-3.6, -6.69) * mm});
            skLineSegment(sketch, "E7.60.0", {"start": v(-3.16, -6.8) * mm, "end": v(-3.29, -6.84) * mm});
            skArc(sketch, "E7.60.1", {"start": v(-3.16, -6.8) * mm, "mid": v(-3.25, -6.76) * mm, "end": v(-3.34, -6.71) * mm});
            skLineSegment(sketch, "E7.60.2", {"start": v(-3.34, -6.71) * mm, "end": v(-3.3, -6.84) * mm});
            skPoint(sketch, "E7.60.3", {"position": v(-3.3, -6.85) * mm});
            skArc(sketch, "E7.60.4", {"start": v(-3.3, -6.84) * mm, "mid": v(-3.3, -6.84) * mm, "end": v(-3.29, -6.84) * mm});
            skLineSegment(sketch, "E7.61.0", {"start": v(-2.86, -6.94) * mm, "end": v(-2.98, -6.98) * mm});
            skArc(sketch, "E7.61.1", {"start": v(-2.86, -6.94) * mm, "mid": v(-2.95, -6.9) * mm, "end": v(-3.04, -6.86) * mm});
            skLineSegment(sketch, "E7.61.2", {"start": v(-3.04, -6.86) * mm, "end": v(-3, -6.98) * mm});
            skPoint(sketch, "E7.61.3", {"position": v(-2.99, -6.99) * mm});
            skArc(sketch, "E7.61.4", {"start": v(-3, -6.98) * mm, "mid": v(-2.99, -6.98) * mm, "end": v(-2.98, -6.98) * mm});
            skLineSegment(sketch, "E7.62.0", {"start": v(-2.54, -7.06) * mm, "end": v(-2.66, -7.11) * mm});
            skArc(sketch, "E7.62.1", {"start": v(-2.54, -7.06) * mm, "mid": v(-2.64, -7.02) * mm, "end": v(-2.73, -6.99) * mm});
            skLineSegment(sketch, "E7.62.2", {"start": v(-2.73, -6.99) * mm, "end": v(-2.68, -7.1) * mm});
            skPoint(sketch, "E7.62.3", {"position": v(-2.67, -7.12) * mm});
            skArc(sketch, "E7.62.4", {"start": v(-2.68, -7.1) * mm, "mid": v(-2.67, -7.11) * mm, "end": v(-2.66, -7.11) * mm});
            skLineSegment(sketch, "E7.63.0", {"start": v(-2.22, -7.16) * mm, "end": v(-2.34, -7.22) * mm});
            skArc(sketch, "E7.63.1", {"start": v(-2.22, -7.16) * mm, "mid": v(-2.32, -7.13) * mm, "end": v(-2.41, -7.1) * mm});
            skLineSegment(sketch, "E7.63.2", {"start": v(-2.41, -7.1) * mm, "end": v(-2.35, -7.22) * mm});
            skPoint(sketch, "E7.63.3", {"position": v(-2.35, -7.23) * mm});
            skArc(sketch, "E7.63.4", {"start": v(-2.35, -7.22) * mm, "mid": v(-2.35, -7.22) * mm, "end": v(-2.34, -7.22) * mm});
            skLineSegment(sketch, "E7.64.0", {"start": v(-1.9, -7.26) * mm, "end": v(-2.01, -7.32) * mm});
            skArc(sketch, "E7.64.1", {"start": v(-1.9, -7.26) * mm, "mid": v(-2, -7.23) * mm, "end": v(-2.1, -7.2) * mm});
            skLineSegment(sketch, "E7.64.2", {"start": v(-2.1, -7.2) * mm, "end": v(-2.03, -7.32) * mm});
            skPoint(sketch, "E7.64.3", {"position": v(-2.02, -7.33) * mm});
            skArc(sketch, "E7.64.4", {"start": v(-2.03, -7.32) * mm, "mid": v(-2.02, -7.32) * mm, "end": v(-2.01, -7.32) * mm});
            skLineSegment(sketch, "E7.65.0", {"start": v(-1.57, -7.33) * mm, "end": v(-1.68, -7.4) * mm});
            skArc(sketch, "E7.65.1", {"start": v(-1.57, -7.33) * mm, "mid": v(-1.67, -7.31) * mm, "end": v(-1.77, -7.29) * mm});
            skLineSegment(sketch, "E7.65.2", {"start": v(-1.77, -7.29) * mm, "end": v(-1.7, -7.4) * mm});
            skPoint(sketch, "E7.65.3", {"position": v(-1.7, -7.4) * mm});
            skArc(sketch, "E7.65.4", {"start": v(-1.7, -7.4) * mm, "mid": v(-1.7, -7.4) * mm, "end": v(-1.68, -7.4) * mm});
            skLineSegment(sketch, "E7.66.0", {"start": v(-1.24, -7.4) * mm, "end": v(-1.35, -7.47) * mm});
            skArc(sketch, "E7.66.1", {"start": v(-1.24, -7.4) * mm, "mid": v(-1.34, -7.38) * mm, "end": v(-1.44, -7.36) * mm});
            skLineSegment(sketch, "E7.66.2", {"start": v(-1.44, -7.36) * mm, "end": v(-1.36, -7.47) * mm});
            skPoint(sketch, "E7.66.3", {"position": v(-1.36, -7.48) * mm});
            skArc(sketch, "E7.66.4", {"start": v(-1.36, -7.47) * mm, "mid": v(-1.36, -7.47) * mm, "end": v(-1.35, -7.47) * mm});
            skLineSegment(sketch, "E7.67.0", {"start": v(-0.9, -7.44) * mm, "end": v(-1.01, -7.52) * mm});
            skArc(sketch, "E7.67.1", {"start": v(-0.9, -7.44) * mm, "mid": v(-1, -7.43) * mm, "end": v(-1.1, -7.42) * mm});
            skLineSegment(sketch, "E7.67.2", {"start": v(-1.1, -7.42) * mm, "end": v(-1.03, -7.52) * mm});
            skPoint(sketch, "E7.67.3", {"position": v(-1.02, -7.53) * mm});
            skArc(sketch, "E7.67.4", {"start": v(-1.03, -7.52) * mm, "mid": v(-1.02, -7.53) * mm, "end": v(-1.01, -7.52) * mm});
            skLineSegment(sketch, "E7.68.0", {"start": v(-0.57, -7.48) * mm, "end": v(-0.67, -7.56) * mm});
            skArc(sketch, "E7.68.1", {"start": v(-0.57, -7.48) * mm, "mid": v(-0.67, -7.47) * mm, "end": v(-0.77, -7.46) * mm});
            skLineSegment(sketch, "E7.68.2", {"start": v(-0.77, -7.46) * mm, "end": v(-0.69, -7.56) * mm});
            skPoint(sketch, "E7.68.3", {"position": v(-0.68, -7.57) * mm});
            skArc(sketch, "E7.68.4", {"start": v(-0.69, -7.56) * mm, "mid": v(-0.68, -7.56) * mm, "end": v(-0.67, -7.56) * mm});
            skLineSegment(sketch, "E7.69.0", {"start": v(-0.24, -7.5) * mm, "end": v(-0.33, -7.58) * mm});
            skArc(sketch, "E7.69.1", {"start": v(-0.24, -7.5) * mm, "mid": v(-0.34, -7.5) * mm, "end": v(-0.44, -7.49) * mm});
            skLineSegment(sketch, "E7.69.2", {"start": v(-0.44, -7.49) * mm, "end": v(-0.35, -7.58) * mm});
            skPoint(sketch, "E7.69.3", {"position": v(-0.34, -7.6) * mm});
            skArc(sketch, "E7.69.4", {"start": v(-0.35, -7.58) * mm, "mid": v(-0.34, -7.59) * mm, "end": v(-0.33, -7.58) * mm});
            skLineSegment(sketch, "E7.70.0", {"start": v(0.1, -7.5) * mm, "end": v(0, -7.6) * mm});
            skArc(sketch, "E7.70.1", {"start": v(0.1, -7.5) * mm, "mid": v(0, -7.5) * mm, "end": v(-0.1, -7.5) * mm});
            skLineSegment(sketch, "E7.70.2", {"start": v(-0.1, -7.5) * mm, "end": v(0, -7.6) * mm});
            skPoint(sketch, "E7.70.3", {"position": v(0, -7.6) * mm});
            skArc(sketch, "E7.70.4", {"start": v(0, -7.6) * mm, "mid": v(0, -7.6) * mm, "end": v(0, -7.6) * mm});
            skLineSegment(sketch, "E7.71.0", {"start": v(0.44, -7.49) * mm, "end": v(0.35, -7.58) * mm});
            skArc(sketch, "E7.71.1", {"start": v(0.44, -7.49) * mm, "mid": v(0.34, -7.5) * mm, "end": v(0.24, -7.5) * mm});
            skLineSegment(sketch, "E7.71.2", {"start": v(0.24, -7.5) * mm, "end": v(0.33, -7.58) * mm});
            skPoint(sketch, "E7.71.3", {"position": v(0.34, -7.6) * mm});
            skArc(sketch, "E7.71.4", {"start": v(0.33, -7.58) * mm, "mid": v(0.34, -7.59) * mm, "end": v(0.35, -7.58) * mm});
            skLineSegment(sketch, "E7.72.0", {"start": v(0.77, -7.46) * mm, "end": v(0.69, -7.56) * mm});
            skArc(sketch, "E7.72.1", {"start": v(0.77, -7.46) * mm, "mid": v(0.67, -7.47) * mm, "end": v(0.57, -7.48) * mm});
            skLineSegment(sketch, "E7.72.2", {"start": v(0.57, -7.48) * mm, "end": v(0.67, -7.56) * mm});
            skPoint(sketch, "E7.72.3", {"position": v(0.68, -7.57) * mm});
            skArc(sketch, "E7.72.4", {"start": v(0.67, -7.56) * mm, "mid": v(0.68, -7.56) * mm, "end": v(0.69, -7.56) * mm});
            skLineSegment(sketch, "E7.73.0", {"start": v(1.1, -7.42) * mm, "end": v(1.03, -7.52) * mm});
            skArc(sketch, "E7.73.1", {"start": v(1.1, -7.42) * mm, "mid": v(1, -7.43) * mm, "end": v(0.9, -7.44) * mm});
            skLineSegment(sketch, "E7.73.2", {"start": v(0.9, -7.44) * mm, "end": v(1.01, -7.52) * mm});
            skPoint(sketch, "E7.73.3", {"position": v(1.02, -7.53) * mm});
            skArc(sketch, "E7.73.4", {"start": v(1.01, -7.52) * mm, "mid": v(1.02, -7.53) * mm, "end": v(1.03, -7.52) * mm});
            skLineSegment(sketch, "E7.74.0", {"start": v(1.44, -7.36) * mm, "end": v(1.36, -7.47) * mm});
            skArc(sketch, "E7.74.1", {"start": v(1.44, -7.36) * mm, "mid": v(1.34, -7.38) * mm, "end": v(1.24, -7.4) * mm});
            skLineSegment(sketch, "E7.74.2", {"start": v(1.24, -7.4) * mm, "end": v(1.35, -7.47) * mm});
            skPoint(sketch, "E7.74.3", {"position": v(1.36, -7.48) * mm});
            skArc(sketch, "E7.74.4", {"start": v(1.35, -7.47) * mm, "mid": v(1.36, -7.47) * mm, "end": v(1.36, -7.47) * mm});
            skLineSegment(sketch, "E7.75.0", {"start": v(1.77, -7.29) * mm, "end": v(1.7, -7.4) * mm});
            skArc(sketch, "E7.75.1", {"start": v(1.77, -7.29) * mm, "mid": v(1.67, -7.31) * mm, "end": v(1.57, -7.33) * mm});
            skLineSegment(sketch, "E7.75.2", {"start": v(1.57, -7.33) * mm, "end": v(1.68, -7.4) * mm});
            skPoint(sketch, "E7.75.3", {"position": v(1.7, -7.4) * mm});
            skArc(sketch, "E7.75.4", {"start": v(1.68, -7.4) * mm, "mid": v(1.7, -7.4) * mm, "end": v(1.7, -7.4) * mm});
            skLineSegment(sketch, "E7.76.0", {"start": v(2.1, -7.2) * mm, "end": v(2.03, -7.32) * mm});
            skArc(sketch, "E7.76.1", {"start": v(2.1, -7.2) * mm, "mid": v(2, -7.23) * mm, "end": v(1.9, -7.26) * mm});
            skLineSegment(sketch, "E7.76.2", {"start": v(1.9, -7.26) * mm, "end": v(2.01, -7.32) * mm});
            skPoint(sketch, "E7.76.3", {"position": v(2.02, -7.33) * mm});
            skArc(sketch, "E7.76.4", {"start": v(2.01, -7.32) * mm, "mid": v(2.02, -7.32) * mm, "end": v(2.03, -7.32) * mm});
            skLineSegment(sketch, "E7.77.0", {"start": v(2.41, -7.1) * mm, "end": v(2.35, -7.22) * mm});
            skArc(sketch, "E7.77.1", {"start": v(2.41, -7.1) * mm, "mid": v(2.32, -7.13) * mm, "end": v(2.22, -7.16) * mm});
            skLineSegment(sketch, "E7.77.2", {"start": v(2.22, -7.16) * mm, "end": v(2.34, -7.22) * mm});
            skPoint(sketch, "E7.77.3", {"position": v(2.35, -7.23) * mm});
            skArc(sketch, "E7.77.4", {"start": v(2.34, -7.22) * mm, "mid": v(2.35, -7.22) * mm, "end": v(2.35, -7.22) * mm});
            skLineSegment(sketch, "E7.78.0", {"start": v(2.73, -6.99) * mm, "end": v(2.68, -7.1) * mm});
            skArc(sketch, "E7.78.1", {"start": v(2.73, -6.99) * mm, "mid": v(2.64, -7.02) * mm, "end": v(2.54, -7.06) * mm});
            skLineSegment(sketch, "E7.78.2", {"start": v(2.54, -7.06) * mm, "end": v(2.66, -7.11) * mm});
            skPoint(sketch, "E7.78.3", {"position": v(2.67, -7.12) * mm});
            skArc(sketch, "E7.78.4", {"start": v(2.66, -7.11) * mm, "mid": v(2.67, -7.11) * mm, "end": v(2.68, -7.1) * mm});
            skLineSegment(sketch, "E7.79.0", {"start": v(3.04, -6.86) * mm, "end": v(3, -6.98) * mm});
            skArc(sketch, "E7.79.1", {"start": v(3.04, -6.86) * mm, "mid": v(2.95, -6.9) * mm, "end": v(2.86, -6.94) * mm});
            skLineSegment(sketch, "E7.79.2", {"start": v(2.86, -6.94) * mm, "end": v(2.98, -6.98) * mm});
            skPoint(sketch, "E7.79.3", {"position": v(2.99, -6.99) * mm});
            skArc(sketch, "E7.79.4", {"start": v(2.98, -6.98) * mm, "mid": v(2.99, -6.98) * mm, "end": v(3, -6.98) * mm});
            skLineSegment(sketch, "E7.80.0", {"start": v(3.34, -6.71) * mm, "end": v(3.3, -6.84) * mm});
            skArc(sketch, "E7.80.1", {"start": v(3.34, -6.71) * mm, "mid": v(3.25, -6.76) * mm, "end": v(3.16, -6.8) * mm});
            skLineSegment(sketch, "E7.80.2", {"start": v(3.16, -6.8) * mm, "end": v(3.29, -6.84) * mm});
            skPoint(sketch, "E7.80.3", {"position": v(3.3, -6.85) * mm});
            skArc(sketch, "E7.80.4", {"start": v(3.29, -6.84) * mm, "mid": v(3.3, -6.84) * mm, "end": v(3.3, -6.84) * mm});
            skLineSegment(sketch, "E7.81.0", {"start": v(3.64, -6.56) * mm, "end": v(3.6, -6.68) * mm});
            skArc(sketch, "E7.81.1", {"start": v(3.64, -6.56) * mm, "mid": v(3.55, -6.6) * mm, "end": v(3.47, -6.65) * mm});
            skLineSegment(sketch, "E7.81.2", {"start": v(3.47, -6.65) * mm, "end": v(3.6, -6.69) * mm});
            skPoint(sketch, "E7.81.3", {"position": v(3.6, -6.7) * mm});
            skArc(sketch, "E7.81.4", {"start": v(3.6, -6.69) * mm, "mid": v(3.6, -6.69) * mm, "end": v(3.6, -6.68) * mm});
            skLineSegment(sketch, "E7.82.0", {"start": v(3.93, -6.39) * mm, "end": v(3.9, -6.51) * mm});
            skArc(sketch, "E7.82.1", {"start": v(3.93, -6.39) * mm, "mid": v(3.85, -6.44) * mm, "end": v(3.76, -6.49) * mm});
            skLineSegment(sketch, "E7.82.2", {"start": v(3.76, -6.49) * mm, "end": v(3.89, -6.52) * mm});
            skPoint(sketch, "E7.82.3", {"position": v(3.9, -6.52) * mm});
            skArc(sketch, "E7.82.4", {"start": v(3.89, -6.52) * mm, "mid": v(3.9, -6.52) * mm, "end": v(3.9, -6.51) * mm});
            skLineSegment(sketch, "E7.83.0", {"start": v(4.21, -6.2) * mm, "end": v(4.19, -6.33) * mm});
            skArc(sketch, "E7.83.1", {"start": v(4.21, -6.2) * mm, "mid": v(4.13, -6.26) * mm, "end": v(4.05, -6.31) * mm});
            skLineSegment(sketch, "E7.83.2", {"start": v(4.05, -6.31) * mm, "end": v(4.18, -6.34) * mm});
            skPoint(sketch, "E7.83.3", {"position": v(4.19, -6.34) * mm});
            skArc(sketch, "E7.83.4", {"start": v(4.18, -6.34) * mm, "mid": v(4.18, -6.34) * mm, "end": v(4.19, -6.33) * mm});
            skLineSegment(sketch, "E7.84.0", {"start": v(4.49, -6) * mm, "end": v(4.47, -6.14) * mm});
            skArc(sketch, "E7.84.1", {"start": v(4.49, -6) * mm, "mid": v(4.4, -6.07) * mm, "end": v(4.33, -6.13) * mm});
            skLineSegment(sketch, "E7.84.2", {"start": v(4.33, -6.13) * mm, "end": v(4.46, -6.15) * mm});
            skPoint(sketch, "E7.84.3", {"position": v(4.47, -6.15) * mm});
            skArc(sketch, "E7.84.4", {"start": v(4.46, -6.15) * mm, "mid": v(4.46, -6.14) * mm, "end": v(4.47, -6.14) * mm});
            skLineSegment(sketch, "E7.85.0", {"start": v(4.75, -5.8) * mm, "end": v(4.74, -5.93) * mm});
            skArc(sketch, "E7.85.1", {"start": v(4.75, -5.8) * mm, "mid": v(4.68, -5.86) * mm, "end": v(4.6, -5.93) * mm});
            skLineSegment(sketch, "E7.85.2", {"start": v(4.6, -5.93) * mm, "end": v(4.73, -5.94) * mm});
            skPoint(sketch, "E7.85.3", {"position": v(4.74, -5.94) * mm});
            skArc(sketch, "E7.85.4", {"start": v(4.73, -5.94) * mm, "mid": v(4.74, -5.94) * mm, "end": v(4.74, -5.93) * mm});
            skLineSegment(sketch, "E7.86.0", {"start": v(5, -5.58) * mm, "end": v(5, -5.71) * mm});
            skArc(sketch, "E7.86.1", {"start": v(5, -5.58) * mm, "mid": v(4.93, -5.65) * mm, "end": v(4.86, -5.71) * mm});
            skLineSegment(sketch, "E7.86.2", {"start": v(4.86, -5.71) * mm, "end": v(4.99, -5.72) * mm});
            skPoint(sketch, "E7.86.3", {"position": v(5, -5.72) * mm});
            skArc(sketch, "E7.86.4", {"start": v(4.99, -5.72) * mm, "mid": v(5, -5.72) * mm, "end": v(5, -5.71) * mm});
            skLineSegment(sketch, "E7.87.0", {"start": v(5.25, -5.35) * mm, "end": v(5.25, -5.48) * mm});
            skArc(sketch, "E7.87.1", {"start": v(5.25, -5.35) * mm, "mid": v(5.18, -5.42) * mm, "end": v(5.11, -5.49) * mm});
            skLineSegment(sketch, "E7.87.2", {"start": v(5.11, -5.49) * mm, "end": v(5.24, -5.5) * mm});
            skPoint(sketch, "E7.87.3", {"position": v(5.25, -5.5) * mm});
            skArc(sketch, "E7.87.4", {"start": v(5.24, -5.5) * mm, "mid": v(5.25, -5.49) * mm, "end": v(5.25, -5.48) * mm});
            skLineSegment(sketch, "E7.88.0", {"start": v(5.49, -5.11) * mm, "end": v(5.5, -5.24) * mm});
            skArc(sketch, "E7.88.1", {"start": v(5.49, -5.11) * mm, "mid": v(5.42, -5.18) * mm, "end": v(5.35, -5.25) * mm});
            skLineSegment(sketch, "E7.88.2", {"start": v(5.35, -5.25) * mm, "end": v(5.48, -5.25) * mm});
            skPoint(sketch, "E7.88.3", {"position": v(5.5, -5.25) * mm});
            skArc(sketch, "E7.88.4", {"start": v(5.48, -5.25) * mm, "mid": v(5.49, -5.25) * mm, "end": v(5.5, -5.24) * mm});
            skLineSegment(sketch, "E7.89.0", {"start": v(5.71, -4.86) * mm, "end": v(5.72, -4.99) * mm});
            skArc(sketch, "E7.89.1", {"start": v(5.71, -4.86) * mm, "mid": v(5.65, -4.93) * mm, "end": v(5.58, -5) * mm});
            skLineSegment(sketch, "E7.89.2", {"start": v(5.58, -5) * mm, "end": v(5.71, -5) * mm});
            skPoint(sketch, "E7.89.3", {"position": v(5.72, -5) * mm});
            skArc(sketch, "E7.89.4", {"start": v(5.71, -5) * mm, "mid": v(5.72, -5) * mm, "end": v(5.72, -4.99) * mm});
            skLineSegment(sketch, "E7.90.0", {"start": v(5.93, -4.6) * mm, "end": v(5.94, -4.73) * mm});
            skArc(sketch, "E7.90.1", {"start": v(5.93, -4.6) * mm, "mid": v(5.86, -4.68) * mm, "end": v(5.8, -4.75) * mm});
            skLineSegment(sketch, "E7.90.2", {"start": v(5.8, -4.75) * mm, "end": v(5.93, -4.74) * mm});
            skPoint(sketch, "E7.90.3", {"position": v(5.94, -4.74) * mm});
            skArc(sketch, "E7.90.4", {"start": v(5.93, -4.74) * mm, "mid": v(5.94, -4.74) * mm, "end": v(5.94, -4.73) * mm});
            skLineSegment(sketch, "E7.91.0", {"start": v(6.13, -4.33) * mm, "end": v(6.15, -4.46) * mm});
            skArc(sketch, "E7.91.1", {"start": v(6.13, -4.33) * mm, "mid": v(6.07, -4.4) * mm, "end": v(6, -4.49) * mm});
            skLineSegment(sketch, "E7.91.2", {"start": v(6, -4.49) * mm, "end": v(6.14, -4.47) * mm});
            skPoint(sketch, "E7.91.3", {"position": v(6.15, -4.47) * mm});
            skArc(sketch, "E7.91.4", {"start": v(6.14, -4.47) * mm, "mid": v(6.14, -4.46) * mm, "end": v(6.15, -4.46) * mm});
            skLineSegment(sketch, "E7.92.0", {"start": v(6.31, -4.05) * mm, "end": v(6.34, -4.18) * mm});
            skArc(sketch, "E7.92.1", {"start": v(6.31, -4.05) * mm, "mid": v(6.26, -4.13) * mm, "end": v(6.2, -4.21) * mm});
            skLineSegment(sketch, "E7.92.2", {"start": v(6.2, -4.21) * mm, "end": v(6.33, -4.19) * mm});
            skPoint(sketch, "E7.92.3", {"position": v(6.34, -4.19) * mm});
            skArc(sketch, "E7.92.4", {"start": v(6.33, -4.19) * mm, "mid": v(6.34, -4.18) * mm, "end": v(6.34, -4.18) * mm});
            skLineSegment(sketch, "E7.93.0", {"start": v(6.49, -3.76) * mm, "end": v(6.52, -3.89) * mm});
            skArc(sketch, "E7.93.1", {"start": v(6.49, -3.76) * mm, "mid": v(6.44, -3.85) * mm, "end": v(6.39, -3.93) * mm});
            skLineSegment(sketch, "E7.93.2", {"start": v(6.39, -3.93) * mm, "end": v(6.51, -3.9) * mm});
            skPoint(sketch, "E7.93.3", {"position": v(6.52, -3.9) * mm});
            skArc(sketch, "E7.93.4", {"start": v(6.51, -3.9) * mm, "mid": v(6.52, -3.9) * mm, "end": v(6.52, -3.89) * mm});
            skLineSegment(sketch, "E7.94.0", {"start": v(6.65, -3.47) * mm, "end": v(6.69, -3.6) * mm});
            skArc(sketch, "E7.94.1", {"start": v(6.65, -3.47) * mm, "mid": v(6.6, -3.55) * mm, "end": v(6.56, -3.64) * mm});
            skLineSegment(sketch, "E7.94.2", {"start": v(6.56, -3.64) * mm, "end": v(6.68, -3.6) * mm});
            skPoint(sketch, "E7.94.3", {"position": v(6.7, -3.6) * mm});
            skArc(sketch, "E7.94.4", {"start": v(6.68, -3.6) * mm, "mid": v(6.69, -3.6) * mm, "end": v(6.69, -3.6) * mm});
            skLineSegment(sketch, "E7.95.0", {"start": v(6.8, -3.16) * mm, "end": v(6.84, -3.29) * mm});
            skArc(sketch, "E7.95.1", {"start": v(6.8, -3.16) * mm, "mid": v(6.76, -3.25) * mm, "end": v(6.71, -3.34) * mm});
            skLineSegment(sketch, "E7.95.2", {"start": v(6.71, -3.34) * mm, "end": v(6.84, -3.3) * mm});
            skPoint(sketch, "E7.95.3", {"position": v(6.85, -3.3) * mm});
            skArc(sketch, "E7.95.4", {"start": v(6.84, -3.3) * mm, "mid": v(6.84, -3.3) * mm, "end": v(6.84, -3.29) * mm});
            skLineSegment(sketch, "E7.96.0", {"start": v(6.94, -2.86) * mm, "end": v(6.98, -2.98) * mm});
            skArc(sketch, "E7.96.1", {"start": v(6.94, -2.86) * mm, "mid": v(6.9, -2.95) * mm, "end": v(6.86, -3.04) * mm});
            skLineSegment(sketch, "E7.96.2", {"start": v(6.86, -3.04) * mm, "end": v(6.98, -3) * mm});
            skPoint(sketch, "E7.96.3", {"position": v(6.99, -2.99) * mm});
            skArc(sketch, "E7.96.4", {"start": v(6.98, -3) * mm, "mid": v(6.98, -2.99) * mm, "end": v(6.98, -2.98) * mm});
            skLineSegment(sketch, "E7.97.0", {"start": v(7.06, -2.54) * mm, "end": v(7.11, -2.66) * mm});
            skArc(sketch, "E7.97.1", {"start": v(7.06, -2.54) * mm, "mid": v(7.02, -2.64) * mm, "end": v(6.99, -2.73) * mm});
            skLineSegment(sketch, "E7.97.2", {"start": v(6.99, -2.73) * mm, "end": v(7.1, -2.68) * mm});
            skPoint(sketch, "E7.97.3", {"position": v(7.12, -2.67) * mm});
            skArc(sketch, "E7.97.4", {"start": v(7.1, -2.68) * mm, "mid": v(7.11, -2.67) * mm, "end": v(7.11, -2.66) * mm});
            skLineSegment(sketch, "E7.98.0", {"start": v(7.16, -2.22) * mm, "end": v(7.22, -2.34) * mm});
            skArc(sketch, "E7.98.1", {"start": v(7.16, -2.22) * mm, "mid": v(7.13, -2.32) * mm, "end": v(7.1, -2.41) * mm});
            skLineSegment(sketch, "E7.98.2", {"start": v(7.1, -2.41) * mm, "end": v(7.22, -2.35) * mm});
            skPoint(sketch, "E7.98.3", {"position": v(7.23, -2.35) * mm});
            skArc(sketch, "E7.98.4", {"start": v(7.22, -2.35) * mm, "mid": v(7.22, -2.35) * mm, "end": v(7.22, -2.34) * mm});
            skLineSegment(sketch, "E7.99.0", {"start": v(7.26, -1.9) * mm, "end": v(7.32, -2.01) * mm});
            skArc(sketch, "E7.99.1", {"start": v(7.26, -1.9) * mm, "mid": v(7.23, -2) * mm, "end": v(7.2, -2.1) * mm});
            skLineSegment(sketch, "E7.99.2", {"start": v(7.2, -2.1) * mm, "end": v(7.32, -2.03) * mm});
            skPoint(sketch, "E7.99.3", {"position": v(7.33, -2.02) * mm});
            skArc(sketch, "E7.99.4", {"start": v(7.32, -2.03) * mm, "mid": v(7.32, -2.02) * mm, "end": v(7.32, -2.01) * mm});
            skLineSegment(sketch, "E7.100.0", {"start": v(7.33, -1.57) * mm, "end": v(7.4, -1.68) * mm});
            skArc(sketch, "E7.100.1", {"start": v(7.33, -1.57) * mm, "mid": v(7.31, -1.67) * mm, "end": v(7.29, -1.77) * mm});
            skLineSegment(sketch, "E7.100.2", {"start": v(7.29, -1.77) * mm, "end": v(7.4, -1.7) * mm});
            skPoint(sketch, "E7.100.3", {"position": v(7.4, -1.7) * mm});
            skArc(sketch, "E7.100.4", {"start": v(7.4, -1.7) * mm, "mid": v(7.4, -1.7) * mm, "end": v(7.4, -1.68) * mm});
            skLineSegment(sketch, "E7.101.0", {"start": v(7.4, -1.24) * mm, "end": v(7.47, -1.35) * mm});
            skArc(sketch, "E7.101.1", {"start": v(7.4, -1.24) * mm, "mid": v(7.38, -1.34) * mm, "end": v(7.36, -1.44) * mm});
            skLineSegment(sketch, "E7.101.2", {"start": v(7.36, -1.44) * mm, "end": v(7.47, -1.36) * mm});
            skPoint(sketch, "E7.101.3", {"position": v(7.48, -1.36) * mm});
            skArc(sketch, "E7.101.4", {"start": v(7.47, -1.36) * mm, "mid": v(7.47, -1.36) * mm, "end": v(7.47, -1.35) * mm});
            skLineSegment(sketch, "E7.102.0", {"start": v(7.44, -0.9) * mm, "end": v(7.52, -1.01) * mm});
            skArc(sketch, "E7.102.1", {"start": v(7.44, -0.9) * mm, "mid": v(7.43, -1) * mm, "end": v(7.42, -1.1) * mm});
            skLineSegment(sketch, "E7.102.2", {"start": v(7.42, -1.1) * mm, "end": v(7.52, -1.03) * mm});
            skPoint(sketch, "E7.102.3", {"position": v(7.53, -1.02) * mm});
            skArc(sketch, "E7.102.4", {"start": v(7.52, -1.03) * mm, "mid": v(7.53, -1.02) * mm, "end": v(7.52, -1.01) * mm});
            skLineSegment(sketch, "E7.103.0", {"start": v(7.48, -0.57) * mm, "end": v(7.56, -0.67) * mm});
            skArc(sketch, "E7.103.1", {"start": v(7.48, -0.57) * mm, "mid": v(7.47, -0.67) * mm, "end": v(7.46, -0.77) * mm});
            skLineSegment(sketch, "E7.103.2", {"start": v(7.46, -0.77) * mm, "end": v(7.56, -0.69) * mm});
            skPoint(sketch, "E7.103.3", {"position": v(7.57, -0.68) * mm});
            skArc(sketch, "E7.103.4", {"start": v(7.56, -0.69) * mm, "mid": v(7.56, -0.68) * mm, "end": v(7.56, -0.67) * mm});
            skLineSegment(sketch, "E7.104.0", {"start": v(7.5, -0.24) * mm, "end": v(7.58, -0.33) * mm});
            skArc(sketch, "E7.104.1", {"start": v(7.5, -0.24) * mm, "mid": v(7.5, -0.34) * mm, "end": v(7.49, -0.44) * mm});
            skLineSegment(sketch, "E7.104.2", {"start": v(7.49, -0.44) * mm, "end": v(7.58, -0.35) * mm});
            skPoint(sketch, "E7.104.3", {"position": v(7.6, -0.34) * mm});
            skArc(sketch, "E7.104.4", {"start": v(7.58, -0.35) * mm, "mid": v(7.59, -0.34) * mm, "end": v(7.58, -0.33) * mm});
            skLineSegment(sketch, "E7.105.0", {"start": v(7.5, 0.1) * mm, "end": v(7.6, 0) * mm});
            skArc(sketch, "E7.105.1", {"start": v(7.5, 0.1) * mm, "mid": v(7.5, 0) * mm, "end": v(7.5, -0.1) * mm});
            skLineSegment(sketch, "E7.105.2", {"start": v(7.5, -0.1) * mm, "end": v(7.6, 0) * mm});
            skPoint(sketch, "E7.105.3", {"position": v(7.6, 0) * mm});
            skArc(sketch, "E7.105.4", {"start": v(7.6, 0) * mm, "mid": v(7.6, 0) * mm, "end": v(7.6, 0) * mm});
            skLineSegment(sketch, "E7.106.0", {"start": v(7.49, 0.44) * mm, "end": v(7.58, 0.35) * mm});
            skArc(sketch, "E7.106.1", {"start": v(7.49, 0.44) * mm, "mid": v(7.5, 0.34) * mm, "end": v(7.5, 0.24) * mm});
            skLineSegment(sketch, "E7.106.2", {"start": v(7.5, 0.24) * mm, "end": v(7.58, 0.33) * mm});
            skPoint(sketch, "E7.106.3", {"position": v(7.6, 0.34) * mm});
            skArc(sketch, "E7.106.4", {"start": v(7.58, 0.33) * mm, "mid": v(7.59, 0.34) * mm, "end": v(7.58, 0.35) * mm});
            skLineSegment(sketch, "E7.107.0", {"start": v(7.46, 0.77) * mm, "end": v(7.56, 0.69) * mm});
            skArc(sketch, "E7.107.1", {"start": v(7.46, 0.77) * mm, "mid": v(7.47, 0.67) * mm, "end": v(7.48, 0.57) * mm});
            skLineSegment(sketch, "E7.107.2", {"start": v(7.48, 0.57) * mm, "end": v(7.56, 0.67) * mm});
            skPoint(sketch, "E7.107.3", {"position": v(7.57, 0.68) * mm});
            skArc(sketch, "E7.107.4", {"start": v(7.56, 0.67) * mm, "mid": v(7.56, 0.68) * mm, "end": v(7.56, 0.69) * mm});
            skLineSegment(sketch, "E7.108.0", {"start": v(7.42, 1.1) * mm, "end": v(7.52, 1.03) * mm});
            skArc(sketch, "E7.108.1", {"start": v(7.42, 1.1) * mm, "mid": v(7.43, 1) * mm, "end": v(7.44, 0.9) * mm});
            skLineSegment(sketch, "E7.108.2", {"start": v(7.44, 0.9) * mm, "end": v(7.52, 1.01) * mm});
            skPoint(sketch, "E7.108.3", {"position": v(7.53, 1.02) * mm});
            skArc(sketch, "E7.108.4", {"start": v(7.52, 1.01) * mm, "mid": v(7.53, 1.02) * mm, "end": v(7.52, 1.03) * mm});
            skLineSegment(sketch, "E7.109.0", {"start": v(7.36, 1.44) * mm, "end": v(7.47, 1.36) * mm});
            skArc(sketch, "E7.109.1", {"start": v(7.36, 1.44) * mm, "mid": v(7.38, 1.34) * mm, "end": v(7.4, 1.24) * mm});
            skLineSegment(sketch, "E7.109.2", {"start": v(7.4, 1.24) * mm, "end": v(7.47, 1.35) * mm});
            skPoint(sketch, "E7.109.3", {"position": v(7.48, 1.36) * mm});
            skArc(sketch, "E7.109.4", {"start": v(7.47, 1.35) * mm, "mid": v(7.47, 1.36) * mm, "end": v(7.47, 1.36) * mm});
            skLineSegment(sketch, "E7.110.0", {"start": v(7.29, 1.77) * mm, "end": v(7.4, 1.7) * mm});
            skArc(sketch, "E7.110.1", {"start": v(7.29, 1.77) * mm, "mid": v(7.31, 1.67) * mm, "end": v(7.33, 1.57) * mm});
            skLineSegment(sketch, "E7.110.2", {"start": v(7.33, 1.57) * mm, "end": v(7.4, 1.68) * mm});
            skPoint(sketch, "E7.110.3", {"position": v(7.4, 1.7) * mm});
            skArc(sketch, "E7.110.4", {"start": v(7.4, 1.68) * mm, "mid": v(7.4, 1.7) * mm, "end": v(7.4, 1.7) * mm});
            skLineSegment(sketch, "E7.111.0", {"start": v(7.2, 2.1) * mm, "end": v(7.32, 2.03) * mm});
            skArc(sketch, "E7.111.1", {"start": v(7.2, 2.1) * mm, "mid": v(7.23, 2) * mm, "end": v(7.26, 1.9) * mm});
            skLineSegment(sketch, "E7.111.2", {"start": v(7.26, 1.9) * mm, "end": v(7.32, 2.01) * mm});
            skPoint(sketch, "E7.111.3", {"position": v(7.33, 2.02) * mm});
            skArc(sketch, "E7.111.4", {"start": v(7.32, 2.01) * mm, "mid": v(7.32, 2.02) * mm, "end": v(7.32, 2.03) * mm});
            skLineSegment(sketch, "E7.112.0", {"start": v(7.1, 2.41) * mm, "end": v(7.22, 2.35) * mm});
            skArc(sketch, "E7.112.1", {"start": v(7.1, 2.41) * mm, "mid": v(7.13, 2.32) * mm, "end": v(7.16, 2.22) * mm});
            skLineSegment(sketch, "E7.112.2", {"start": v(7.16, 2.22) * mm, "end": v(7.22, 2.34) * mm});
            skPoint(sketch, "E7.112.3", {"position": v(7.23, 2.35) * mm});
            skArc(sketch, "E7.112.4", {"start": v(7.22, 2.34) * mm, "mid": v(7.22, 2.35) * mm, "end": v(7.22, 2.35) * mm});
            skLineSegment(sketch, "E7.113.0", {"start": v(6.99, 2.73) * mm, "end": v(7.1, 2.68) * mm});
            skArc(sketch, "E7.113.1", {"start": v(6.99, 2.73) * mm, "mid": v(7.02, 2.64) * mm, "end": v(7.06, 2.54) * mm});
            skLineSegment(sketch, "E7.113.2", {"start": v(7.06, 2.54) * mm, "end": v(7.11, 2.66) * mm});
            skPoint(sketch, "E7.113.3", {"position": v(7.12, 2.67) * mm});
            skArc(sketch, "E7.113.4", {"start": v(7.11, 2.66) * mm, "mid": v(7.11, 2.67) * mm, "end": v(7.1, 2.68) * mm});
            skLineSegment(sketch, "E7.114.0", {"start": v(6.86, 3.04) * mm, "end": v(6.98, 3) * mm});
            skArc(sketch, "E7.114.1", {"start": v(6.86, 3.04) * mm, "mid": v(6.9, 2.95) * mm, "end": v(6.94, 2.86) * mm});
            skLineSegment(sketch, "E7.114.2", {"start": v(6.94, 2.86) * mm, "end": v(6.98, 2.98) * mm});
            skPoint(sketch, "E7.114.3", {"position": v(6.99, 2.99) * mm});
            skArc(sketch, "E7.114.4", {"start": v(6.98, 2.98) * mm, "mid": v(6.98, 2.99) * mm, "end": v(6.98, 3) * mm});
            skLineSegment(sketch, "E7.115.0", {"start": v(6.71, 3.34) * mm, "end": v(6.84, 3.3) * mm});
            skArc(sketch, "E7.115.1", {"start": v(6.71, 3.34) * mm, "mid": v(6.76, 3.25) * mm, "end": v(6.8, 3.16) * mm});
            skLineSegment(sketch, "E7.115.2", {"start": v(6.8, 3.16) * mm, "end": v(6.84, 3.29) * mm});
            skPoint(sketch, "E7.115.3", {"position": v(6.85, 3.3) * mm});
            skArc(sketch, "E7.115.4", {"start": v(6.84, 3.29) * mm, "mid": v(6.84, 3.3) * mm, "end": v(6.84, 3.3) * mm});
            skLineSegment(sketch, "E7.116.0", {"start": v(6.56, 3.64) * mm, "end": v(6.68, 3.6) * mm});
            skArc(sketch, "E7.116.1", {"start": v(6.56, 3.64) * mm, "mid": v(6.6, 3.55) * mm, "end": v(6.65, 3.47) * mm});
            skLineSegment(sketch, "E7.116.2", {"start": v(6.65, 3.47) * mm, "end": v(6.69, 3.6) * mm});
            skPoint(sketch, "E7.116.3", {"position": v(6.7, 3.6) * mm});
            skArc(sketch, "E7.116.4", {"start": v(6.69, 3.6) * mm, "mid": v(6.69, 3.6) * mm, "end": v(6.68, 3.6) * mm});
            skLineSegment(sketch, "E7.117.0", {"start": v(6.39, 3.93) * mm, "end": v(6.51, 3.9) * mm});
            skArc(sketch, "E7.117.1", {"start": v(6.39, 3.93) * mm, "mid": v(6.44, 3.85) * mm, "end": v(6.49, 3.76) * mm});
            skLineSegment(sketch, "E7.117.2", {"start": v(6.49, 3.76) * mm, "end": v(6.52, 3.89) * mm});
            skPoint(sketch, "E7.117.3", {"position": v(6.52, 3.9) * mm});
            skArc(sketch, "E7.117.4", {"start": v(6.52, 3.89) * mm, "mid": v(6.52, 3.9) * mm, "end": v(6.51, 3.9) * mm});
            skLineSegment(sketch, "E7.118.0", {"start": v(6.2, 4.21) * mm, "end": v(6.33, 4.19) * mm});
            skArc(sketch, "E7.118.1", {"start": v(6.2, 4.21) * mm, "mid": v(6.26, 4.13) * mm, "end": v(6.31, 4.05) * mm});
            skLineSegment(sketch, "E7.118.2", {"start": v(6.31, 4.05) * mm, "end": v(6.34, 4.18) * mm});
            skPoint(sketch, "E7.118.3", {"position": v(6.34, 4.19) * mm});
            skArc(sketch, "E7.118.4", {"start": v(6.34, 4.18) * mm, "mid": v(6.34, 4.18) * mm, "end": v(6.33, 4.19) * mm});
            skLineSegment(sketch, "E7.119.0", {"start": v(6, 4.49) * mm, "end": v(6.14, 4.47) * mm});
            skArc(sketch, "E7.119.1", {"start": v(6, 4.49) * mm, "mid": v(6.07, 4.4) * mm, "end": v(6.13, 4.33) * mm});
            skLineSegment(sketch, "E7.119.2", {"start": v(6.13, 4.33) * mm, "end": v(6.15, 4.46) * mm});
            skPoint(sketch, "E7.119.3", {"position": v(6.15, 4.47) * mm});
            skArc(sketch, "E7.119.4", {"start": v(6.15, 4.46) * mm, "mid": v(6.14, 4.46) * mm, "end": v(6.14, 4.47) * mm});
            skLineSegment(sketch, "E7.120.0", {"start": v(5.8, 4.75) * mm, "end": v(5.93, 4.74) * mm});
            skArc(sketch, "E7.120.1", {"start": v(5.8, 4.75) * mm, "mid": v(5.86, 4.68) * mm, "end": v(5.93, 4.6) * mm});
            skLineSegment(sketch, "E7.120.2", {"start": v(5.93, 4.6) * mm, "end": v(5.94, 4.73) * mm});
            skPoint(sketch, "E7.120.3", {"position": v(5.94, 4.74) * mm});
            skArc(sketch, "E7.120.4", {"start": v(5.94, 4.73) * mm, "mid": v(5.94, 4.74) * mm, "end": v(5.93, 4.74) * mm});
            skLineSegment(sketch, "E7.121.0", {"start": v(5.58, 5) * mm, "end": v(5.71, 5) * mm});
            skArc(sketch, "E7.121.1", {"start": v(5.58, 5) * mm, "mid": v(5.65, 4.93) * mm, "end": v(5.71, 4.86) * mm});
            skLineSegment(sketch, "E7.121.2", {"start": v(5.71, 4.86) * mm, "end": v(5.72, 4.99) * mm});
            skPoint(sketch, "E7.121.3", {"position": v(5.72, 5) * mm});
            skArc(sketch, "E7.121.4", {"start": v(5.72, 4.99) * mm, "mid": v(5.72, 5) * mm, "end": v(5.71, 5) * mm});
            skLineSegment(sketch, "E7.122.0", {"start": v(5.35, 5.25) * mm, "end": v(5.48, 5.25) * mm});
            skArc(sketch, "E7.122.1", {"start": v(5.35, 5.25) * mm, "mid": v(5.42, 5.18) * mm, "end": v(5.49, 5.11) * mm});
            skLineSegment(sketch, "E7.122.2", {"start": v(5.49, 5.11) * mm, "end": v(5.5, 5.24) * mm});
            skPoint(sketch, "E7.122.3", {"position": v(5.5, 5.25) * mm});
            skArc(sketch, "E7.122.4", {"start": v(5.5, 5.24) * mm, "mid": v(5.49, 5.25) * mm, "end": v(5.48, 5.25) * mm});
            skLineSegment(sketch, "E7.123.0", {"start": v(5.11, 5.49) * mm, "end": v(5.24, 5.5) * mm});
            skArc(sketch, "E7.123.1", {"start": v(5.11, 5.49) * mm, "mid": v(5.18, 5.42) * mm, "end": v(5.25, 5.35) * mm});
            skLineSegment(sketch, "E7.123.2", {"start": v(5.25, 5.35) * mm, "end": v(5.25, 5.48) * mm});
            skPoint(sketch, "E7.123.3", {"position": v(5.25, 5.5) * mm});
            skArc(sketch, "E7.123.4", {"start": v(5.25, 5.48) * mm, "mid": v(5.25, 5.49) * mm, "end": v(5.24, 5.5) * mm});
            skLineSegment(sketch, "E7.124.0", {"start": v(4.86, 5.71) * mm, "end": v(4.99, 5.72) * mm});
            skArc(sketch, "E7.124.1", {"start": v(4.86, 5.71) * mm, "mid": v(4.93, 5.65) * mm, "end": v(5, 5.58) * mm});
            skLineSegment(sketch, "E7.124.2", {"start": v(5, 5.58) * mm, "end": v(5, 5.71) * mm});
            skPoint(sketch, "E7.124.3", {"position": v(5, 5.72) * mm});
            skArc(sketch, "E7.124.4", {"start": v(5, 5.71) * mm, "mid": v(5, 5.72) * mm, "end": v(4.99, 5.72) * mm});
            skLineSegment(sketch, "E7.125.0", {"start": v(4.6, 5.93) * mm, "end": v(4.73, 5.94) * mm});
            skArc(sketch, "E7.125.1", {"start": v(4.6, 5.93) * mm, "mid": v(4.68, 5.86) * mm, "end": v(4.75, 5.8) * mm});
            skLineSegment(sketch, "E7.125.2", {"start": v(4.75, 5.8) * mm, "end": v(4.74, 5.93) * mm});
            skPoint(sketch, "E7.125.3", {"position": v(4.74, 5.94) * mm});
            skArc(sketch, "E7.125.4", {"start": v(4.74, 5.93) * mm, "mid": v(4.74, 5.94) * mm, "end": v(4.73, 5.94) * mm});
            skLineSegment(sketch, "E7.126.0", {"start": v(4.33, 6.13) * mm, "end": v(4.46, 6.15) * mm});
            skArc(sketch, "E7.126.1", {"start": v(4.33, 6.13) * mm, "mid": v(4.4, 6.07) * mm, "end": v(4.49, 6) * mm});
            skLineSegment(sketch, "E7.126.2", {"start": v(4.49, 6) * mm, "end": v(4.47, 6.14) * mm});
            skPoint(sketch, "E7.126.3", {"position": v(4.47, 6.15) * mm});
            skArc(sketch, "E7.126.4", {"start": v(4.47, 6.14) * mm, "mid": v(4.46, 6.14) * mm, "end": v(4.46, 6.15) * mm});
            skLineSegment(sketch, "E7.127.0", {"start": v(4.05, 6.31) * mm, "end": v(4.18, 6.34) * mm});
            skArc(sketch, "E7.127.1", {"start": v(4.05, 6.31) * mm, "mid": v(4.13, 6.26) * mm, "end": v(4.21, 6.2) * mm});
            skLineSegment(sketch, "E7.127.2", {"start": v(4.21, 6.2) * mm, "end": v(4.19, 6.33) * mm});
            skPoint(sketch, "E7.127.3", {"position": v(4.19, 6.34) * mm});
            skArc(sketch, "E7.127.4", {"start": v(4.19, 6.33) * mm, "mid": v(4.18, 6.34) * mm, "end": v(4.18, 6.34) * mm});
            skLineSegment(sketch, "E7.128.0", {"start": v(3.76, 6.49) * mm, "end": v(3.89, 6.52) * mm});
            skArc(sketch, "E7.128.1", {"start": v(3.76, 6.49) * mm, "mid": v(3.85, 6.44) * mm, "end": v(3.93, 6.39) * mm});
            skLineSegment(sketch, "E7.128.2", {"start": v(3.93, 6.39) * mm, "end": v(3.9, 6.51) * mm});
            skPoint(sketch, "E7.128.3", {"position": v(3.9, 6.52) * mm});
            skArc(sketch, "E7.128.4", {"start": v(3.9, 6.51) * mm, "mid": v(3.9, 6.52) * mm, "end": v(3.89, 6.52) * mm});
            skLineSegment(sketch, "E7.129.0", {"start": v(3.47, 6.65) * mm, "end": v(3.6, 6.69) * mm});
            skArc(sketch, "E7.129.1", {"start": v(3.47, 6.65) * mm, "mid": v(3.55, 6.6) * mm, "end": v(3.64, 6.56) * mm});
            skLineSegment(sketch, "E7.129.2", {"start": v(3.64, 6.56) * mm, "end": v(3.6, 6.68) * mm});
            skPoint(sketch, "E7.129.3", {"position": v(3.6, 6.7) * mm});
            skArc(sketch, "E7.129.4", {"start": v(3.6, 6.68) * mm, "mid": v(3.6, 6.69) * mm, "end": v(3.6, 6.69) * mm});
            skLineSegment(sketch, "E7.130.0", {"start": v(3.16, 6.8) * mm, "end": v(3.29, 6.84) * mm});
            skArc(sketch, "E7.130.1", {"start": v(3.16, 6.8) * mm, "mid": v(3.25, 6.76) * mm, "end": v(3.34, 6.71) * mm});
            skLineSegment(sketch, "E7.130.2", {"start": v(3.34, 6.71) * mm, "end": v(3.3, 6.84) * mm});
            skPoint(sketch, "E7.130.3", {"position": v(3.3, 6.85) * mm});
            skArc(sketch, "E7.130.4", {"start": v(3.3, 6.84) * mm, "mid": v(3.3, 6.84) * mm, "end": v(3.29, 6.84) * mm});
            skLineSegment(sketch, "E7.131.0", {"start": v(2.86, 6.94) * mm, "end": v(2.98, 6.98) * mm});
            skArc(sketch, "E7.131.1", {"start": v(2.86, 6.94) * mm, "mid": v(2.95, 6.9) * mm, "end": v(3.04, 6.86) * mm});
            skLineSegment(sketch, "E7.131.2", {"start": v(3.04, 6.86) * mm, "end": v(3, 6.98) * mm});
            skPoint(sketch, "E7.131.3", {"position": v(2.99, 6.99) * mm});
            skArc(sketch, "E7.131.4", {"start": v(3, 6.98) * mm, "mid": v(2.99, 6.98) * mm, "end": v(2.98, 6.98) * mm});
            skLineSegment(sketch, "E7.132.0", {"start": v(2.54, 7.06) * mm, "end": v(2.66, 7.11) * mm});
            skArc(sketch, "E7.132.1", {"start": v(2.54, 7.06) * mm, "mid": v(2.64, 7.02) * mm, "end": v(2.73, 6.99) * mm});
            skLineSegment(sketch, "E7.132.2", {"start": v(2.73, 6.99) * mm, "end": v(2.68, 7.1) * mm});
            skPoint(sketch, "E7.132.3", {"position": v(2.67, 7.12) * mm});
            skArc(sketch, "E7.132.4", {"start": v(2.68, 7.1) * mm, "mid": v(2.67, 7.11) * mm, "end": v(2.66, 7.11) * mm});
            skLineSegment(sketch, "E7.133.0", {"start": v(2.22, 7.16) * mm, "end": v(2.34, 7.22) * mm});
            skArc(sketch, "E7.133.1", {"start": v(2.22, 7.16) * mm, "mid": v(2.32, 7.13) * mm, "end": v(2.41, 7.1) * mm});
            skLineSegment(sketch, "E7.133.2", {"start": v(2.41, 7.1) * mm, "end": v(2.35, 7.22) * mm});
            skPoint(sketch, "E7.133.3", {"position": v(2.35, 7.23) * mm});
            skArc(sketch, "E7.133.4", {"start": v(2.35, 7.22) * mm, "mid": v(2.35, 7.22) * mm, "end": v(2.34, 7.22) * mm});
            skLineSegment(sketch, "E7.134.0", {"start": v(1.9, 7.26) * mm, "end": v(2.01, 7.32) * mm});
            skArc(sketch, "E7.134.1", {"start": v(1.9, 7.26) * mm, "mid": v(2, 7.23) * mm, "end": v(2.1, 7.2) * mm});
            skLineSegment(sketch, "E7.134.2", {"start": v(2.1, 7.2) * mm, "end": v(2.03, 7.32) * mm});
            skPoint(sketch, "E7.134.3", {"position": v(2.02, 7.33) * mm});
            skArc(sketch, "E7.134.4", {"start": v(2.03, 7.32) * mm, "mid": v(2.02, 7.32) * mm, "end": v(2.01, 7.32) * mm});
            skLineSegment(sketch, "E7.135.0", {"start": v(1.57, 7.33) * mm, "end": v(1.68, 7.4) * mm});
            skArc(sketch, "E7.135.1", {"start": v(1.57, 7.33) * mm, "mid": v(1.67, 7.31) * mm, "end": v(1.77, 7.29) * mm});
            skLineSegment(sketch, "E7.135.2", {"start": v(1.77, 7.29) * mm, "end": v(1.7, 7.4) * mm});
            skPoint(sketch, "E7.135.3", {"position": v(1.7, 7.4) * mm});
            skArc(sketch, "E7.135.4", {"start": v(1.7, 7.4) * mm, "mid": v(1.7, 7.4) * mm, "end": v(1.68, 7.4) * mm});
            skLineSegment(sketch, "E7.136.0", {"start": v(1.24, 7.4) * mm, "end": v(1.35, 7.47) * mm});
            skArc(sketch, "E7.136.1", {"start": v(1.24, 7.4) * mm, "mid": v(1.34, 7.38) * mm, "end": v(1.44, 7.36) * mm});
            skLineSegment(sketch, "E7.136.2", {"start": v(1.44, 7.36) * mm, "end": v(1.36, 7.47) * mm});
            skPoint(sketch, "E7.136.3", {"position": v(1.36, 7.48) * mm});
            skArc(sketch, "E7.136.4", {"start": v(1.36, 7.47) * mm, "mid": v(1.36, 7.47) * mm, "end": v(1.35, 7.47) * mm});
            skLineSegment(sketch, "E7.137.0", {"start": v(0.9, 7.44) * mm, "end": v(1.01, 7.52) * mm});
            skArc(sketch, "E7.137.1", {"start": v(0.9, 7.44) * mm, "mid": v(1, 7.43) * mm, "end": v(1.1, 7.42) * mm});
            skLineSegment(sketch, "E7.137.2", {"start": v(1.1, 7.42) * mm, "end": v(1.03, 7.52) * mm});
            skPoint(sketch, "E7.137.3", {"position": v(1.02, 7.53) * mm});
            skArc(sketch, "E7.137.4", {"start": v(1.03, 7.52) * mm, "mid": v(1.02, 7.53) * mm, "end": v(1.01, 7.52) * mm});
            skLineSegment(sketch, "E7.138.0", {"start": v(0.57, 7.48) * mm, "end": v(0.67, 7.56) * mm});
            skArc(sketch, "E7.138.1", {"start": v(0.57, 7.48) * mm, "mid": v(0.67, 7.47) * mm, "end": v(0.77, 7.46) * mm});
            skLineSegment(sketch, "E7.138.2", {"start": v(0.77, 7.46) * mm, "end": v(0.69, 7.56) * mm});
            skPoint(sketch, "E7.138.3", {"position": v(0.68, 7.57) * mm});
            skArc(sketch, "E7.138.4", {"start": v(0.69, 7.56) * mm, "mid": v(0.68, 7.56) * mm, "end": v(0.67, 7.56) * mm});
            skLineSegment(sketch, "E7.139.0", {"start": v(0.24, 7.5) * mm, "end": v(0.33, 7.58) * mm});
            skArc(sketch, "E7.139.1", {"start": v(0.24, 7.5) * mm, "mid": v(0.34, 7.5) * mm, "end": v(0.44, 7.49) * mm});
            skLineSegment(sketch, "E7.139.2", {"start": v(0.44, 7.49) * mm, "end": v(0.35, 7.58) * mm});
            skPoint(sketch, "E7.139.3", {"position": v(0.34, 7.6) * mm});
            skArc(sketch, "E7.139.4", {"start": v(0.35, 7.58) * mm, "mid": v(0.34, 7.59) * mm, "end": v(0.33, 7.58) * mm});
            skSolve(sketch);
        }
        {
            var Q0;
            Q0 = qSketchRegion(id + "F0", true);
            extrude(context, id + "F1", {"entities" : qUnion([Q0]), "depth" : 3 * mm, "offsetDistance" : 25 * mm});
        }
        {
            var Q0;
            Q0=makeQuery(id+"F1.opExtrude","CAP_FACE",FACE,{"disambiguationData":[OSD([sQuery(id+"F0.wireOp",EDGE,"E0"),sQuery(id+"F0.wireOp",EDGE,"E1"),sQuery(id+"F0.wireOp",EDGE,"E3"),sQuery(id+"F0.wireOp",EDGE,"E4"),sQuery(id+"F0.wireOp",EDGE,"E5.filletArc"),sQuery(id+"F0.wireOp",EDGE,"E7.1.0"),sQuery(id+"F0.wireOp",EDGE,"E7.1.2"),sQuery(id+"F0.wireOp",EDGE,"E7.1.4"),sQuery(id+"F0.wireOp",EDGE,"E7.2.0"),sQuery(id+"F0.wireOp",EDGE,"E7.2.2"),sQuery(id+"F0.wireOp",EDGE,"E7.2.4"),sQuery(id+"F0.wireOp",EDGE,"E7.3.0"),sQuery(id+"F0.wireOp",EDGE,"E7.3.2"),sQuery(id+"F0.wireOp",EDGE,"E7.3.4"),sQuery(id+"F0.wireOp",EDGE,"E7.4.0"),sQuery(id+"F0.wireOp",EDGE,"E7.4.2"),sQuery(id+"F0.wireOp",EDGE,"E7.4.4"),sQuery(id+"F0.wireOp",EDGE,"E7.5.0"),sQuery(id+"F0.wireOp",EDGE,"E7.5.2"),sQuery(id+"F0.wireOp",EDGE,"E7.5.4"),sQuery(id+"F0.wireOp",EDGE,"E7.6.0"),sQuery(id+"F0.wireOp",EDGE,"E7.6.2"),sQuery(id+"F0.wireOp",EDGE,"E7.6.4"),sQuery(id+"F0.wireOp",EDGE,"E7.7.0"),sQuery(id+"F0.wireOp",EDGE,"E7.7.2"),sQuery(id+"F0.wireOp",EDGE,"E7.7.4"),sQuery(id+"F0.wireOp",EDGE,"E7.8.0"),sQuery(id+"F0.wireOp",EDGE,"E7.8.2"),sQuery(id+"F0.wireOp",EDGE,"E7.8.4"),sQuery(id+"F0.wireOp",EDGE,"E7.9.0"),sQuery(id+"F0.wireOp",EDGE,"E7.9.2"),sQuery(id+"F0.wireOp",EDGE,"E7.9.4"),sQuery(id+"F0.wireOp",EDGE,"E7.10.0"),sQuery(id+"F0.wireOp",EDGE,"E7.10.2"),sQuery(id+"F0.wireOp",EDGE,"E7.10.4"),sQuery(id+"F0.wireOp",EDGE,"E7.11.0"),sQuery(id+"F0.wireOp",EDGE,"E7.11.2"),sQuery(id+"F0.wireOp",EDGE,"E7.11.4"),sQuery(id+"F0.wireOp",EDGE,"E7.12.0"),sQuery(id+"F0.wireOp",EDGE,"E7.12.2"),sQuery(id+"F0.wireOp",EDGE,"E7.12.4"),sQuery(id+"F0.wireOp",EDGE,"E7.13.0"),sQuery(id+"F0.wireOp",EDGE,"E7.13.2"),sQuery(id+"F0.wireOp",EDGE,"E7.13.4"),sQuery(id+"F0.wireOp",EDGE,"E7.14.0"),sQuery(id+"F0.wireOp",EDGE,"E7.14.2"),sQuery(id+"F0.wireOp",EDGE,"E7.14.4"),sQuery(id+"F0.wireOp",EDGE,"E7.15.0"),sQuery(id+"F0.wireOp",EDGE,"E7.15.2"),sQuery(id+"F0.wireOp",EDGE,"E7.15.4"),sQuery(id+"F0.wireOp",EDGE,"E7.16.0"),sQuery(id+"F0.wireOp",EDGE,"E7.16.2"),sQuery(id+"F0.wireOp",EDGE,"E7.16.4"),sQuery(id+"F0.wireOp",EDGE,"E7.17.0"),sQuery(id+"F0.wireOp",EDGE,"E7.17.2"),sQuery(id+"F0.wireOp",EDGE,"E7.17.4"),sQuery(id+"F0.wireOp",EDGE,"E7.18.0"),sQuery(id+"F0.wireOp",EDGE,"E7.18.2"),sQuery(id+"F0.wireOp",EDGE,"E7.18.4"),sQuery(id+"F0.wireOp",EDGE,"E7.19.0"),sQuery(id+"F0.wireOp",EDGE,"E7.19.2"),sQuery(id+"F0.wireOp",EDGE,"E7.19.4"),sQuery(id+"F0.wireOp",EDGE,"E7.20.0"),sQuery(id+"F0.wireOp",EDGE,"E7.20.2"),sQuery(id+"F0.wireOp",EDGE,"E7.20.4"),sQuery(id+"F0.wireOp",EDGE,"E7.21.0"),sQuery(id+"F0.wireOp",EDGE,"E7.21.2"),sQuery(id+"F0.wireOp",EDGE,"E7.21.4"),sQuery(id+"F0.wireOp",EDGE,"E7.22.0"),sQuery(id+"F0.wireOp",EDGE,"E7.22.2"),sQuery(id+"F0.wireOp",EDGE,"E7.22.4"),sQuery(id+"F0.wireOp",EDGE,"E7.23.0"),sQuery(id+"F0.wireOp",EDGE,"E7.23.2"),sQuery(id+"F0.wireOp",EDGE,"E7.23.4"),sQuery(id+"F0.wireOp",EDGE,"E7.24.0"),sQuery(id+"F0.wireOp",EDGE,"E7.24.2"),sQuery(id+"F0.wireOp",EDGE,"E7.24.4"),sQuery(id+"F0.wireOp",EDGE,"E7.25.0"),sQuery(id+"F0.wireOp",EDGE,"E7.25.2"),sQuery(id+"F0.wireOp",EDGE,"E7.25.4"),sQuery(id+"F0.wireOp",EDGE,"E7.26.0"),sQuery(id+"F0.wireOp",EDGE,"E7.26.2"),sQuery(id+"F0.wireOp",EDGE,"E7.26.4"),sQuery(id+"F0.wireOp",EDGE,"E7.27.0"),sQuery(id+"F0.wireOp",EDGE,"E7.27.2"),sQuery(id+"F0.wireOp",EDGE,"E7.27.4"),sQuery(id+"F0.wireOp",EDGE,"E7.28.0"),sQuery(id+"F0.wireOp",EDGE,"E7.28.2"),sQuery(id+"F0.wireOp",EDGE,"E7.28.4"),sQuery(id+"F0.wireOp",EDGE,"E7.29.0"),sQuery(id+"F0.wireOp",EDGE,"E7.29.2"),sQuery(id+"F0.wireOp",EDGE,"E7.29.4"),sQuery(id+"F0.wireOp",EDGE,"E7.30.0"),sQuery(id+"F0.wireOp",EDGE,"E7.30.2"),sQuery(id+"F0.wireOp",EDGE,"E7.30.4"),sQuery(id+"F0.wireOp",EDGE,"E7.31.0"),sQuery(id+"F0.wireOp",EDGE,"E7.31.2"),sQuery(id+"F0.wireOp",EDGE,"E7.31.4"),sQuery(id+"F0.wireOp",EDGE,"E7.32.0"),sQuery(id+"F0.wireOp",EDGE,"E7.32.2"),sQuery(id+"F0.wireOp",EDGE,"E7.32.4"),sQuery(id+"F0.wireOp",EDGE,"E7.33.0"),sQuery(id+"F0.wireOp",EDGE,"E7.33.2"),sQuery(id+"F0.wireOp",EDGE,"E7.33.4"),sQuery(id+"F0.wireOp",EDGE,"E7.34.0"),sQuery(id+"F0.wireOp",EDGE,"E7.34.2"),sQuery(id+"F0.wireOp",EDGE,"E7.34.4"),sQuery(id+"F0.wireOp",EDGE,"E7.35.0"),sQuery(id+"F0.wireOp",EDGE,"E7.35.2"),sQuery(id+"F0.wireOp",EDGE,"E7.35.4"),sQuery(id+"F0.wireOp",EDGE,"E7.36.0"),sQuery(id+"F0.wireOp",EDGE,"E7.36.2"),sQuery(id+"F0.wireOp",EDGE,"E7.36.4"),sQuery(id+"F0.wireOp",EDGE,"E7.37.0"),sQuery(id+"F0.wireOp",EDGE,"E7.37.2"),sQuery(id+"F0.wireOp",EDGE,"E7.37.4"),sQuery(id+"F0.wireOp",EDGE,"E7.38.0"),sQuery(id+"F0.wireOp",EDGE,"E7.38.2"),sQuery(id+"F0.wireOp",EDGE,"E7.38.4"),sQuery(id+"F0.wireOp",EDGE,"E7.39.0"),sQuery(id+"F0.wireOp",EDGE,"E7.39.2"),sQuery(id+"F0.wireOp",EDGE,"E7.39.4"),sQuery(id+"F0.wireOp",EDGE,"E7.40.0"),sQuery(id+"F0.wireOp",EDGE,"E7.40.2"),sQuery(id+"F0.wireOp",EDGE,"E7.40.4"),sQuery(id+"F0.wireOp",EDGE,"E7.41.0"),sQuery(id+"F0.wireOp",EDGE,"E7.41.2"),sQuery(id+"F0.wireOp",EDGE,"E7.41.4"),sQuery(id+"F0.wireOp",EDGE,"E7.42.0"),sQuery(id+"F0.wireOp",EDGE,"E7.42.2"),sQuery(id+"F0.wireOp",EDGE,"E7.42.4"),sQuery(id+"F0.wireOp",EDGE,"E7.43.0"),sQuery(id+"F0.wireOp",EDGE,"E7.43.2"),sQuery(id+"F0.wireOp",EDGE,"E7.43.4"),sQuery(id+"F0.wireOp",EDGE,"E7.44.0"),sQuery(id+"F0.wireOp",EDGE,"E7.44.2"),sQuery(id+"F0.wireOp",EDGE,"E7.44.4"),sQuery(id+"F0.wireOp",EDGE,"E7.45.0"),sQuery(id+"F0.wireOp",EDGE,"E7.45.2"),sQuery(id+"F0.wireOp",EDGE,"E7.45.4"),sQuery(id+"F0.wireOp",EDGE,"E7.46.0"),sQuery(id+"F0.wireOp",EDGE,"E7.46.2"),sQuery(id+"F0.wireOp",EDGE,"E7.46.4"),sQuery(id+"F0.wireOp",EDGE,"E7.47.0"),sQuery(id+"F0.wireOp",EDGE,"E7.47.2"),sQuery(id+"F0.wireOp",EDGE,"E7.47.4"),sQuery(id+"F0.wireOp",EDGE,"E7.48.0"),sQuery(id+"F0.wireOp",EDGE,"E7.48.2"),sQuery(id+"F0.wireOp",EDGE,"E7.48.4"),sQuery(id+"F0.wireOp",EDGE,"E7.49.0"),sQuery(id+"F0.wireOp",EDGE,"E7.49.2"),sQuery(id+"F0.wireOp",EDGE,"E7.49.4"),sQuery(id+"F0.wireOp",EDGE,"E7.50.0"),sQuery(id+"F0.wireOp",EDGE,"E7.50.2"),sQuery(id+"F0.wireOp",EDGE,"E7.50.4"),sQuery(id+"F0.wireOp",EDGE,"E7.51.0"),sQuery(id+"F0.wireOp",EDGE,"E7.51.2"),sQuery(id+"F0.wireOp",EDGE,"E7.51.4"),sQuery(id+"F0.wireOp",EDGE,"E7.52.0"),sQuery(id+"F0.wireOp",EDGE,"E7.52.2"),sQuery(id+"F0.wireOp",EDGE,"E7.52.4"),sQuery(id+"F0.wireOp",EDGE,"E7.53.0"),sQuery(id+"F0.wireOp",EDGE,"E7.53.2"),sQuery(id+"F0.wireOp",EDGE,"E7.53.4"),sQuery(id+"F0.wireOp",EDGE,"E7.54.0"),sQuery(id+"F0.wireOp",EDGE,"E7.54.2"),sQuery(id+"F0.wireOp",EDGE,"E7.54.4"),sQuery(id+"F0.wireOp",EDGE,"E7.55.0"),sQuery(id+"F0.wireOp",EDGE,"E7.55.2"),sQuery(id+"F0.wireOp",EDGE,"E7.55.4"),sQuery(id+"F0.wireOp",EDGE,"E7.56.0"),sQuery(id+"F0.wireOp",EDGE,"E7.56.2"),sQuery(id+"F0.wireOp",EDGE,"E7.56.4"),sQuery(id+"F0.wireOp",EDGE,"E7.57.0"),sQuery(id+"F0.wireOp",EDGE,"E7.57.2"),sQuery(id+"F0.wireOp",EDGE,"E7.57.4"),sQuery(id+"F0.wireOp",EDGE,"E7.58.0"),sQuery(id+"F0.wireOp",EDGE,"E7.58.2"),sQuery(id+"F0.wireOp",EDGE,"E7.58.4"),sQuery(id+"F0.wireOp",EDGE,"E7.59.0"),sQuery(id+"F0.wireOp",EDGE,"E7.59.2"),sQuery(id+"F0.wireOp",EDGE,"E7.59.4"),sQuery(id+"F0.wireOp",EDGE,"E7.60.0"),sQuery(id+"F0.wireOp",EDGE,"E7.60.2"),sQuery(id+"F0.wireOp",EDGE,"E7.60.4"),sQuery(id+"F0.wireOp",EDGE,"E7.61.0"),sQuery(id+"F0.wireOp",EDGE,"E7.61.2"),sQuery(id+"F0.wireOp",EDGE,"E7.61.4"),sQuery(id+"F0.wireOp",EDGE,"E7.62.0"),sQuery(id+"F0.wireOp",EDGE,"E7.62.2"),sQuery(id+"F0.wireOp",EDGE,"E7.62.4"),sQuery(id+"F0.wireOp",EDGE,"E7.63.0"),sQuery(id+"F0.wireOp",EDGE,"E7.63.2"),sQuery(id+"F0.wireOp",EDGE,"E7.63.4"),sQuery(id+"F0.wireOp",EDGE,"E7.64.0"),sQuery(id+"F0.wireOp",EDGE,"E7.64.2"),sQuery(id+"F0.wireOp",EDGE,"E7.64.4"),sQuery(id+"F0.wireOp",EDGE,"E7.65.0"),sQuery(id+"F0.wireOp",EDGE,"E7.65.2"),sQuery(id+"F0.wireOp",EDGE,"E7.65.4"),sQuery(id+"F0.wireOp",EDGE,"E7.66.0"),sQuery(id+"F0.wireOp",EDGE,"E7.66.2"),sQuery(id+"F0.wireOp",EDGE,"E7.66.4"),sQuery(id+"F0.wireOp",EDGE,"E7.67.0"),sQuery(id+"F0.wireOp",EDGE,"E7.67.2"),sQuery(id+"F0.wireOp",EDGE,"E7.67.4"),sQuery(id+"F0.wireOp",EDGE,"E7.68.0"),sQuery(id+"F0.wireOp",EDGE,"E7.68.2"),sQuery(id+"F0.wireOp",EDGE,"E7.68.4"),sQuery(id+"F0.wireOp",EDGE,"E7.69.0"),sQuery(id+"F0.wireOp",EDGE,"E7.69.2"),sQuery(id+"F0.wireOp",EDGE,"E7.69.4"),sQuery(id+"F0.wireOp",EDGE,"E7.70.0"),sQuery(id+"F0.wireOp",EDGE,"E7.70.2"),sQuery(id+"F0.wireOp",EDGE,"E7.70.4"),sQuery(id+"F0.wireOp",EDGE,"E7.71.0"),sQuery(id+"F0.wireOp",EDGE,"E7.71.2"),sQuery(id+"F0.wireOp",EDGE,"E7.71.4"),sQuery(id+"F0.wireOp",EDGE,"E7.72.0"),sQuery(id+"F0.wireOp",EDGE,"E7.72.2"),sQuery(id+"F0.wireOp",EDGE,"E7.72.4"),sQuery(id+"F0.wireOp",EDGE,"E7.73.0"),sQuery(id+"F0.wireOp",EDGE,"E7.73.2"),sQuery(id+"F0.wireOp",EDGE,"E7.73.4"),sQuery(id+"F0.wireOp",EDGE,"E7.74.0"),sQuery(id+"F0.wireOp",EDGE,"E7.74.2"),sQuery(id+"F0.wireOp",EDGE,"E7.74.4"),sQuery(id+"F0.wireOp",EDGE,"E7.75.0"),sQuery(id+"F0.wireOp",EDGE,"E7.75.2"),sQuery(id+"F0.wireOp",EDGE,"E7.75.4"),sQuery(id+"F0.wireOp",EDGE,"E7.76.0"),sQuery(id+"F0.wireOp",EDGE,"E7.76.2"),sQuery(id+"F0.wireOp",EDGE,"E7.76.4"),sQuery(id+"F0.wireOp",EDGE,"E7.77.0"),sQuery(id+"F0.wireOp",EDGE,"E7.77.2"),sQuery(id+"F0.wireOp",EDGE,"E7.77.4"),sQuery(id+"F0.wireOp",EDGE,"E7.78.0"),sQuery(id+"F0.wireOp",EDGE,"E7.78.2"),sQuery(id+"F0.wireOp",EDGE,"E7.78.4"),sQuery(id+"F0.wireOp",EDGE,"E7.79.0"),sQuery(id+"F0.wireOp",EDGE,"E7.79.2"),sQuery(id+"F0.wireOp",EDGE,"E7.79.4"),sQuery(id+"F0.wireOp",EDGE,"E7.80.0"),sQuery(id+"F0.wireOp",EDGE,"E7.80.2"),sQuery(id+"F0.wireOp",EDGE,"E7.80.4"),sQuery(id+"F0.wireOp",EDGE,"E7.81.0"),sQuery(id+"F0.wireOp",EDGE,"E7.81.2"),sQuery(id+"F0.wireOp",EDGE,"E7.81.4"),sQuery(id+"F0.wireOp",EDGE,"E7.82.0"),sQuery(id+"F0.wireOp",EDGE,"E7.82.2"),sQuery(id+"F0.wireOp",EDGE,"E7.82.4"),sQuery(id+"F0.wireOp",EDGE,"E7.83.0"),sQuery(id+"F0.wireOp",EDGE,"E7.83.2"),sQuery(id+"F0.wireOp",EDGE,"E7.83.4"),sQuery(id+"F0.wireOp",EDGE,"E7.84.0"),sQuery(id+"F0.wireOp",EDGE,"E7.84.2"),sQuery(id+"F0.wireOp",EDGE,"E7.84.4"),sQuery(id+"F0.wireOp",EDGE,"E7.85.0"),sQuery(id+"F0.wireOp",EDGE,"E7.85.2"),sQuery(id+"F0.wireOp",EDGE,"E7.85.4"),sQuery(id+"F0.wireOp",EDGE,"E7.86.0"),sQuery(id+"F0.wireOp",EDGE,"E7.86.2"),sQuery(id+"F0.wireOp",EDGE,"E7.86.4"),sQuery(id+"F0.wireOp",EDGE,"E7.87.0"),sQuery(id+"F0.wireOp",EDGE,"E7.87.2"),sQuery(id+"F0.wireOp",EDGE,"E7.87.4"),sQuery(id+"F0.wireOp",EDGE,"E7.88.0"),sQuery(id+"F0.wireOp",EDGE,"E7.88.2"),sQuery(id+"F0.wireOp",EDGE,"E7.88.4"),sQuery(id+"F0.wireOp",EDGE,"E7.89.0"),sQuery(id+"F0.wireOp",EDGE,"E7.89.2"),sQuery(id+"F0.wireOp",EDGE,"E7.89.4"),sQuery(id+"F0.wireOp",EDGE,"E7.90.0"),sQuery(id+"F0.wireOp",EDGE,"E7.90.2"),sQuery(id+"F0.wireOp",EDGE,"E7.90.4"),sQuery(id+"F0.wireOp",EDGE,"E7.91.0"),sQuery(id+"F0.wireOp",EDGE,"E7.91.2"),sQuery(id+"F0.wireOp",EDGE,"E7.91.4"),sQuery(id+"F0.wireOp",EDGE,"E7.92.0"),sQuery(id+"F0.wireOp",EDGE,"E7.92.2"),sQuery(id+"F0.wireOp",EDGE,"E7.92.4"),sQuery(id+"F0.wireOp",EDGE,"E7.93.0"),sQuery(id+"F0.wireOp",EDGE,"E7.93.2"),sQuery(id+"F0.wireOp",EDGE,"E7.93.4"),sQuery(id+"F0.wireOp",EDGE,"E7.94.0"),sQuery(id+"F0.wireOp",EDGE,"E7.94.2"),sQuery(id+"F0.wireOp",EDGE,"E7.94.4"),sQuery(id+"F0.wireOp",EDGE,"E7.95.0"),sQuery(id+"F0.wireOp",EDGE,"E7.95.2"),sQuery(id+"F0.wireOp",EDGE,"E7.95.4"),sQuery(id+"F0.wireOp",EDGE,"E7.96.0"),sQuery(id+"F0.wireOp",EDGE,"E7.96.2"),sQuery(id+"F0.wireOp",EDGE,"E7.96.4"),sQuery(id+"F0.wireOp",EDGE,"E7.97.0"),sQuery(id+"F0.wireOp",EDGE,"E7.97.2"),sQuery(id+"F0.wireOp",EDGE,"E7.97.4"),sQuery(id+"F0.wireOp",EDGE,"E7.98.0"),sQuery(id+"F0.wireOp",EDGE,"E7.98.2"),sQuery(id+"F0.wireOp",EDGE,"E7.98.4"),sQuery(id+"F0.wireOp",EDGE,"E7.99.0"),sQuery(id+"F0.wireOp",EDGE,"E7.99.2"),sQuery(id+"F0.wireOp",EDGE,"E7.99.4"),sQuery(id+"F0.wireOp",EDGE,"E7.100.0"),sQuery(id+"F0.wireOp",EDGE,"E7.100.2"),sQuery(id+"F0.wireOp",EDGE,"E7.100.4"),sQuery(id+"F0.wireOp",EDGE,"E7.101.0"),sQuery(id+"F0.wireOp",EDGE,"E7.101.2"),sQuery(id+"F0.wireOp",EDGE,"E7.101.4"),sQuery(id+"F0.wireOp",EDGE,"E7.102.0"),sQuery(id+"F0.wireOp",EDGE,"E7.102.2"),sQuery(id+"F0.wireOp",EDGE,"E7.102.4"),sQuery(id+"F0.wireOp",EDGE,"E7.103.0"),sQuery(id+"F0.wireOp",EDGE,"E7.103.2"),sQuery(id+"F0.wireOp",EDGE,"E7.103.4"),sQuery(id+"F0.wireOp",EDGE,"E7.104.0"),sQuery(id+"F0.wireOp",EDGE,"E7.104.2"),sQuery(id+"F0.wireOp",EDGE,"E7.104.4"),sQuery(id+"F0.wireOp",EDGE,"E7.105.0"),sQuery(id+"F0.wireOp",EDGE,"E7.105.2"),sQuery(id+"F0.wireOp",EDGE,"E7.105.4"),sQuery(id+"F0.wireOp",EDGE,"E7.106.0"),sQuery(id+"F0.wireOp",EDGE,"E7.106.2"),sQuery(id+"F0.wireOp",EDGE,"E7.106.4"),sQuery(id+"F0.wireOp",EDGE,"E7.107.0"),sQuery(id+"F0.wireOp",EDGE,"E7.107.2"),sQuery(id+"F0.wireOp",EDGE,"E7.107.4"),sQuery(id+"F0.wireOp",EDGE,"E7.108.0"),sQuery(id+"F0.wireOp",EDGE,"E7.108.2"),sQuery(id+"F0.wireOp",EDGE,"E7.108.4"),sQuery(id+"F0.wireOp",EDGE,"E7.109.0"),sQuery(id+"F0.wireOp",EDGE,"E7.109.2"),sQuery(id+"F0.wireOp",EDGE,"E7.109.4"),sQuery(id+"F0.wireOp",EDGE,"E7.110.0"),sQuery(id+"F0.wireOp",EDGE,"E7.110.2"),sQuery(id+"F0.wireOp",EDGE,"E7.110.4"),sQuery(id+"F0.wireOp",EDGE,"E7.111.0"),sQuery(id+"F0.wireOp",EDGE,"E7.111.2"),sQuery(id+"F0.wireOp",EDGE,"E7.111.4"),sQuery(id+"F0.wireOp",EDGE,"E7.112.0"),sQuery(id+"F0.wireOp",EDGE,"E7.112.2"),sQuery(id+"F0.wireOp",EDGE,"E7.112.4"),sQuery(id+"F0.wireOp",EDGE,"E7.113.0"),sQuery(id+"F0.wireOp",EDGE,"E7.113.2"),sQuery(id+"F0.wireOp",EDGE,"E7.113.4"),sQuery(id+"F0.wireOp",EDGE,"E7.114.0"),sQuery(id+"F0.wireOp",EDGE,"E7.114.2"),sQuery(id+"F0.wireOp",EDGE,"E7.114.4"),sQuery(id+"F0.wireOp",EDGE,"E7.115.0"),sQuery(id+"F0.wireOp",EDGE,"E7.115.2"),sQuery(id+"F0.wireOp",EDGE,"E7.115.4"),sQuery(id+"F0.wireOp",EDGE,"E7.116.0"),sQuery(id+"F0.wireOp",EDGE,"E7.116.2"),sQuery(id+"F0.wireOp",EDGE,"E7.116.4"),sQuery(id+"F0.wireOp",EDGE,"E7.117.0"),sQuery(id+"F0.wireOp",EDGE,"E7.117.2"),sQuery(id+"F0.wireOp",EDGE,"E7.117.4"),sQuery(id+"F0.wireOp",EDGE,"E7.118.0"),sQuery(id+"F0.wireOp",EDGE,"E7.118.2"),sQuery(id+"F0.wireOp",EDGE,"E7.118.4"),sQuery(id+"F0.wireOp",EDGE,"E7.119.0"),sQuery(id+"F0.wireOp",EDGE,"E7.119.2"),sQuery(id+"F0.wireOp",EDGE,"E7.119.4"),sQuery(id+"F0.wireOp",EDGE,"E7.120.0"),sQuery(id+"F0.wireOp",EDGE,"E7.120.2"),sQuery(id+"F0.wireOp",EDGE,"E7.120.4"),sQuery(id+"F0.wireOp",EDGE,"E7.121.0"),sQuery(id+"F0.wireOp",EDGE,"E7.121.2"),sQuery(id+"F0.wireOp",EDGE,"E7.121.4"),sQuery(id+"F0.wireOp",EDGE,"E7.122.0"),sQuery(id+"F0.wireOp",EDGE,"E7.122.2"),sQuery(id+"F0.wireOp",EDGE,"E7.122.4"),sQuery(id+"F0.wireOp",EDGE,"E7.123.0"),sQuery(id+"F0.wireOp",EDGE,"E7.123.2"),sQuery(id+"F0.wireOp",EDGE,"E7.123.4"),sQuery(id+"F0.wireOp",EDGE,"E7.124.0"),sQuery(id+"F0.wireOp",EDGE,"E7.124.2"),sQuery(id+"F0.wireOp",EDGE,"E7.124.4"),sQuery(id+"F0.wireOp",EDGE,"E7.125.0"),sQuery(id+"F0.wireOp",EDGE,"E7.125.2"),sQuery(id+"F0.wireOp",EDGE,"E7.125.4"),sQuery(id+"F0.wireOp",EDGE,"E7.126.0"),sQuery(id+"F0.wireOp",EDGE,"E7.126.2"),sQuery(id+"F0.wireOp",EDGE,"E7.126.4"),sQuery(id+"F0.wireOp",EDGE,"E7.127.0"),sQuery(id+"F0.wireOp",EDGE,"E7.127.2"),sQuery(id+"F0.wireOp",EDGE,"E7.127.4"),sQuery(id+"F0.wireOp",EDGE,"E7.128.0"),sQuery(id+"F0.wireOp",EDGE,"E7.128.2"),sQuery(id+"F0.wireOp",EDGE,"E7.128.4"),sQuery(id+"F0.wireOp",EDGE,"E7.129.0"),sQuery(id+"F0.wireOp",EDGE,"E7.129.2"),sQuery(id+"F0.wireOp",EDGE,"E7.129.4"),sQuery(id+"F0.wireOp",EDGE,"E7.130.0"),sQuery(id+"F0.wireOp",EDGE,"E7.130.2"),sQuery(id+"F0.wireOp",EDGE,"E7.130.4"),sQuery(id+"F0.wireOp",EDGE,"E7.131.0"),sQuery(id+"F0.wireOp",EDGE,"E7.131.2"),sQuery(id+"F0.wireOp",EDGE,"E7.131.4"),sQuery(id+"F0.wireOp",EDGE,"E7.132.0"),sQuery(id+"F0.wireOp",EDGE,"E7.132.2"),sQuery(id+"F0.wireOp",EDGE,"E7.132.4"),sQuery(id+"F0.wireOp",EDGE,"E7.133.0"),sQuery(id+"F0.wireOp",EDGE,"E7.133.2"),sQuery(id+"F0.wireOp",EDGE,"E7.133.4"),sQuery(id+"F0.wireOp",EDGE,"E7.134.0"),sQuery(id+"F0.wireOp",EDGE,"E7.134.2"),sQuery(id+"F0.wireOp",EDGE,"E7.134.4"),sQuery(id+"F0.wireOp",EDGE,"E7.135.0"),sQuery(id+"F0.wireOp",EDGE,"E7.135.2"),sQuery(id+"F0.wireOp",EDGE,"E7.135.4"),sQuery(id+"F0.wireOp",EDGE,"E7.136.0"),sQuery(id+"F0.wireOp",EDGE,"E7.136.2"),sQuery(id+"F0.wireOp",EDGE,"E7.136.4"),sQuery(id+"F0.wireOp",EDGE,"E7.137.0"),sQuery(id+"F0.wireOp",EDGE,"E7.137.2"),sQuery(id+"F0.wireOp",EDGE,"E7.137.4"),sQuery(id+"F0.wireOp",EDGE,"E7.138.0"),sQuery(id+"F0.wireOp",EDGE,"E7.138.2"),sQuery(id+"F0.wireOp",EDGE,"E7.138.4"),sQuery(id+"F0.wireOp",EDGE,"E7.139.0"),sQuery(id+"F0.wireOp",EDGE,"E7.139.2"),sQuery(id+"F0.wireOp",EDGE,"E7.139.4")])],"isStart":false});
            var sketch = newSketch(context, id + "F2", { "sketchPlane" : qUnion([Q0])});
            skCircle(sketch, "E8", {"center": v(0, 0) * mm, "radius": 2 * mm});
            skCircle(sketch, "E9", {"center": v(0, 0) * mm, "radius": 4.5 * mm});
            skSolve(sketch);
        }
        {
            var Q0;
            Q0 = qSketchRegion(id + "F2", true);
            extrude(context, id + "F3", {"entities" : qUnion([Q0]), "operationType" : NewBodyOperationType.ADD, "depth" : 0.5 * mm, "offsetDistance" : 25 * mm});
        }
    });
